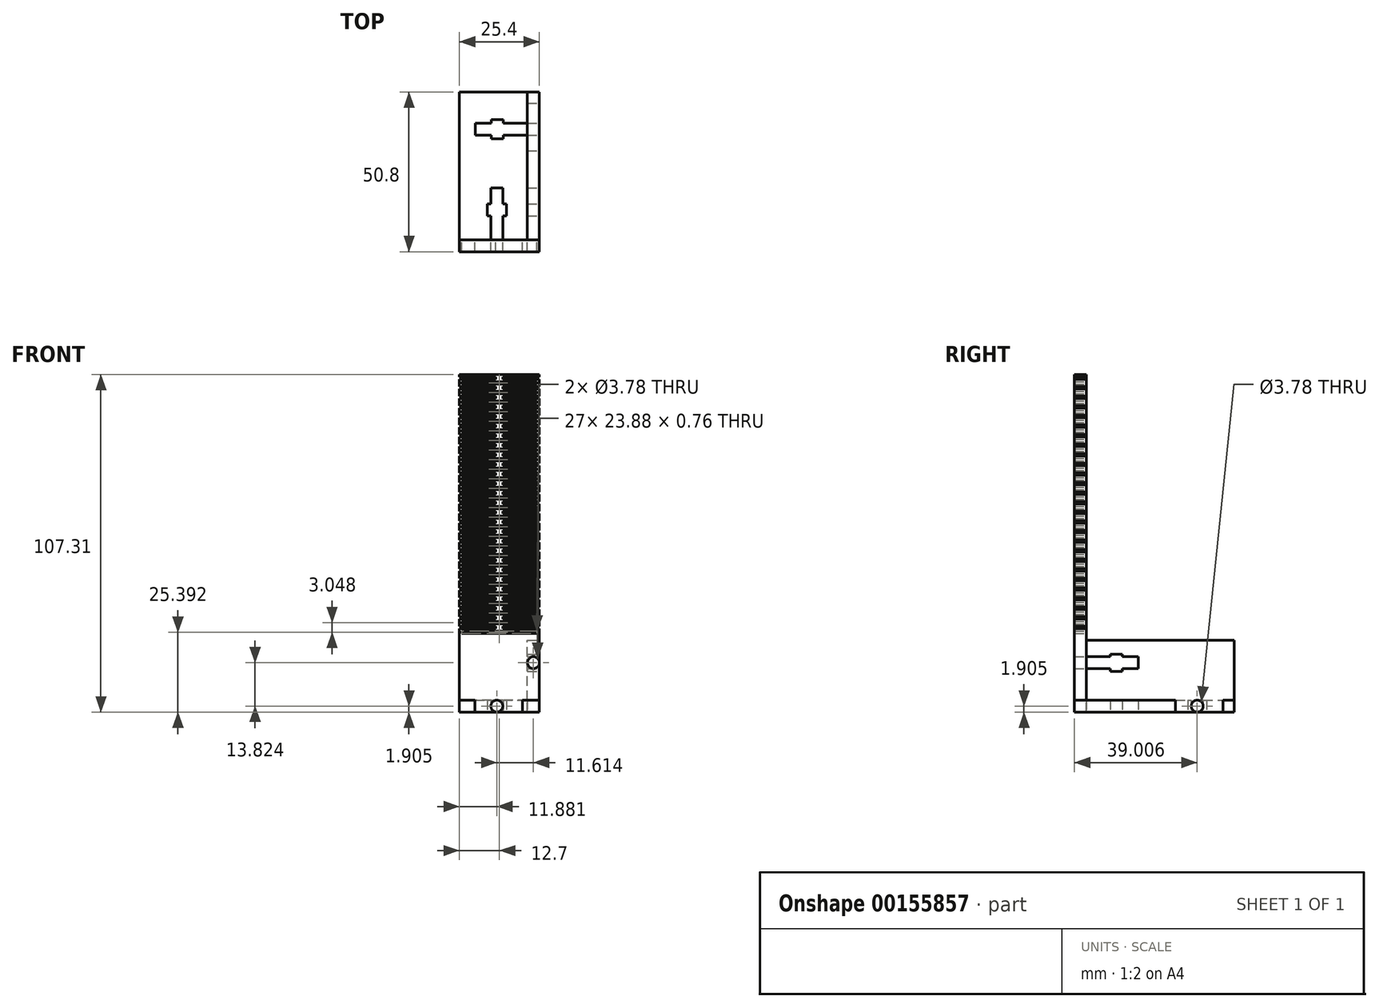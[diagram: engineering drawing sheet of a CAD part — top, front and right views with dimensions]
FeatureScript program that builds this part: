
annotation { "Feature Type Name" : "Feature", "Feature Type Description" : "" }
export const myFeature = defineFeature(function(context is Context, id is Id, definition is map)
    precondition{}
    {
        {
            var Q0;
            Q0=qCreatedBy(makeId("Top.planeOp"),FACE);
            var sketch = newSketch(context, id + "F0", { "sketchPlane" : qUnion([Q0])});
            skLineSegment(sketch, "E0.bottom", {"start": v(-25.4, -50.8) * mm, "end": v(-20.43, -50.8) * mm});
            skLineSegment(sketch, "E0.top", {"start": v(-25.4, 0) * mm, "end": v(0, 0) * mm});
            skLineSegment(sketch, "E0.left", {"start": v(-25.4, -50.8) * mm, "end": v(-25.4, 0) * mm});
            skLineSegment(sketch, "E0.right", {"start": v(0, -50.8) * mm, "end": v(0, -18.7) * mm});
            skLineSegment(sketch, "E1.bottom", {"start": v(-3.8, -9.89) * mm, "end": v(-11.43, -9.89) * mm});
            skLineSegment(sketch, "E1.top", {"start": v(-3.8, -13.7) * mm, "end": v(-11.43, -13.7) * mm});
            skLineSegment(sketch, "E1.right", {"start": v(-20.32, -9.89) * mm, "end": v(-20.32, -13.7) * mm});
            skLineSegment(sketch, "E2.bottom", {"start": v(-15.24, -14.83) * mm, "end": v(-11.43, -14.83) * mm});
            skLineSegment(sketch, "E2.top", {"start": v(-15.24, -8.76) * mm, "end": v(-11.43, -8.76) * mm});
            skLineSegment(sketch, "E2.left", {"start": v(-15.24, -14.83) * mm, "end": v(-15.24, -13.7) * mm});
            skLineSegment(sketch, "E2.right", {"start": v(-11.43, -14.83) * mm, "end": v(-11.43, -13.7) * mm});
            skLineSegment(sketch, "E3.trimOffspring", {"start": v(-11.43, -9.89) * mm, "end": v(-11.43, -8.76) * mm});
            skLineSegment(sketch, "E4.trimOffspring", {"start": v(-15.24, -9.89) * mm, "end": v(-15.24, -8.76) * mm});
            skLineSegment(sketch, "E5.trimOffspring", {"start": v(-15.24, -9.89) * mm, "end": v(-20.32, -9.89) * mm});
            skLineSegment(sketch, "E6.trimOffspring", {"start": v(-15.24, -13.7) * mm, "end": v(-20.32, -13.7) * mm});
            skLineSegment(sketch, "E7.bottom", {"start": v(0, -18.7) * mm, "end": v(-3.8, -18.7) * mm});
            skLineSegment(sketch, "E7.top", {"start": v(0, -3.62) * mm, "end": v(-3.8, -3.62) * mm});
            skLineSegment(sketch, "E7.right", {"start": v(-3.8, -18.7) * mm, "end": v(-3.8, -13.7) * mm});
            skLineSegment(sketch, "E8.trimOffspring", {"start": v(-3.8, -9.89) * mm, "end": v(-3.8, -3.62) * mm});
            skLineSegment(sketch, "E9.trimOffspring", {"start": v(0, -3.62) * mm, "end": v(0, 0) * mm});
            skLineSegment(sketch, "E10.bottom", {"start": v(-11.63, -46.99) * mm, "end": v(-11.63, -39.37) * mm});
            skLineSegment(sketch, "E10.top", {"start": v(-15.44, -46.99) * mm, "end": v(-15.44, -39.37) * mm});
            skLineSegment(sketch, "E10.right", {"start": v(-11.63, -30.48) * mm, "end": v(-15.44, -30.48) * mm});
            skLineSegment(sketch, "E11.bottom", {"start": v(-16.57, -35.56) * mm, "end": v(-16.57, -39.37) * mm});
            skLineSegment(sketch, "E11.top", {"start": v(-10.5, -35.56) * mm, "end": v(-10.5, -39.37) * mm});
            skLineSegment(sketch, "E11.left", {"start": v(-16.57, -35.56) * mm, "end": v(-15.44, -35.56) * mm});
            skLineSegment(sketch, "E11.right", {"start": v(-16.57, -39.37) * mm, "end": v(-15.44, -39.37) * mm});
            skLineSegment(sketch, "E12.trimOffspring", {"start": v(-11.63, -39.37) * mm, "end": v(-10.5, -39.37) * mm});
            skLineSegment(sketch, "E13.trimOffspring", {"start": v(-11.63, -35.56) * mm, "end": v(-10.5, -35.56) * mm});
            skLineSegment(sketch, "E14.trimOffspring", {"start": v(-11.63, -35.56) * mm, "end": v(-11.63, -30.48) * mm});
            skLineSegment(sketch, "E15.trimOffspring", {"start": v(-15.44, -35.56) * mm, "end": v(-15.44, -30.48) * mm});
            skLineSegment(sketch, "E16.bottom", {"start": v(-20.43, -50.8) * mm, "end": v(-20.43, -46.99) * mm});
            skLineSegment(sketch, "E16.top", {"start": v(-5.36, -50.8) * mm, "end": v(-5.36, -46.99) * mm});
            skLineSegment(sketch, "E16.right", {"start": v(-20.43, -46.99) * mm, "end": v(-15.44, -46.99) * mm});
            skLineSegment(sketch, "E17.trimOffspring", {"start": v(-11.63, -46.99) * mm, "end": v(-5.36, -46.99) * mm});
            skLineSegment(sketch, "E18.trimOffspring", {"start": v(-5.36, -50.8) * mm, "end": v(0, -50.8) * mm});
            skSolve(sketch);
        }
        {
            var Q0;
            Q0=makeQuery(id+"F0.imprint","IMPRINT",FACE,{"disambiguationData":[TD([[makeQuery(id+"F0.imprint","IMPRINT",EDGE,{"derivedFrom":sQuery(id+"F0.wireOp",EDGE,"E0.bottom")}),1.0]])]});
            extrude(context, id + "F1", {"entities" : qUnion([Q0]), "depth" : 3.8 * mm});
        }
        {
            var Q0;
            Q0=makeQuery(id+"F1.opExtrude","SWEPT_FACE",FACE,{"disambiguationData":[OSD([sQuery(id+"F0.wireOp",EDGE,"E16.right")])]});
            var sketch = newSketch(context, id + "F2", { "sketchPlane" : qUnion([Q0])});
            skLineSegment(sketch, "E19.bottom", {"start": v(-5.36, 0) * mm, "end": v(-20.43, 0) * mm});
            skLineSegment(sketch, "E20", {"start": v(-20.43, 0) * mm, "end": v(-20.43, 3.81) * mm});
            skLineSegment(sketch, "E21", {"start": v(-20.43, 3.81) * mm, "end": v(-25.4, 3.81) * mm});
            skLineSegment(sketch, "E22.MirrorCS", {"start": v(-5.36, 0) * mm, "end": v(-5.36, 3.81) * mm});
            skLineSegment(sketch, "E23.MirrorCS", {"start": v(-5.36, 3.81) * mm, "end": v(0, 3.81) * mm});
            skCircle(sketch, "E24", {"center": v(-13.52, 1.9) * mm, "radius": 1.9 * mm});
            skLineSegment(sketch, "E25", {"start": v(-20.43, 1.9) * mm, "end": v(-5.36, 1.9) * mm, "construction": true});
            skLineSegment(sketch, "E26", {"start": v(-25.4, 107.3) * mm, "end": v(-12.7, 107.3) * mm});
            skLineSegment(sketch, "E27", {"start": v(-12.7, 107.3) * mm, "end": v(-12.7, -12.92) * mm, "construction": true});
            skLineSegment(sketch, "E28.bottom", {"start": v(-25.4, 106.55) * mm, "end": v(-13.82, 106.55) * mm});
            skLineSegment(sketch, "E28.top", {"start": v(-25.4, 105.78) * mm, "end": v(-13.82, 105.78) * mm});
            skLineSegment(sketch, "E28.right", {"start": v(-13.82, 106.55) * mm, "end": v(-13.82, 105.78) * mm});
            skLineSegment(sketch, "E29.trimOffspring", {"start": v(-25.4, 106.55) * mm, "end": v(-25.4, 107.3) * mm});
            skPoint(sketch, "E30.start.orphan", {"position": v(0, 107.3) * mm});
            skLineSegment(sketch, "E31.MirrorCS", {"start": v(-11.58, 106.55) * mm, "end": v(-11.58, 105.78) * mm});
            skLineSegment(sketch, "E32.MirrorCS", {"start": v(0, 107.3) * mm, "end": v(-12.7, 107.3) * mm});
            skLineSegment(sketch, "E33.MirrorCS", {"start": v(0, 105.78) * mm, "end": v(-11.58, 105.78) * mm});
            skLineSegment(sketch, "E34.MirrorCS", {"start": v(0, 106.55) * mm, "end": v(0, 107.3) * mm});
            skLineSegment(sketch, "E35.MirrorCS", {"start": v(0, 106.55) * mm, "end": v(-11.58, 106.55) * mm});
            skLineSegment(sketch, "E36.bottom", {"start": v(-24.64, 105.02) * mm, "end": v(-0.76, 105.02) * mm});
            skLineSegment(sketch, "E36.top", {"start": v(-24.64, 104.26) * mm, "end": v(-0.76, 104.26) * mm});
            skLineSegment(sketch, "E36.left", {"start": v(-24.64, 105.02) * mm, "end": v(-24.64, 104.26) * mm});
            skLineSegment(sketch, "E36.right", {"start": v(-0.76, 105.02) * mm, "end": v(-0.76, 104.26) * mm});
            skLineSegment(sketch, "E37", {"start": v(-25.4, 105.78) * mm, "end": v(-25.4, 104.26) * mm});
            skLineSegment(sketch, "E38.MirrorCS", {"start": v(-38.1, 107.3) * mm, "end": v(-38.1, -12.92) * mm, "construction": true});
            skLineSegment(sketch, "E39.MirrorCS", {"start": v(0, 105.78) * mm, "end": v(0, 104.26) * mm});
            skLineSegment(sketch, "E40.0.1.0", {"start": v(-0.76, 101.97) * mm, "end": v(-0.76, 101.21) * mm});
            skLineSegment(sketch, "E40.0.1.1", {"start": v(0, 103.5) * mm, "end": v(0, 104.26) * mm});
            skPoint(sketch, "E40.0.1.2", {"position": v(0, 104.26) * mm});
            skLineSegment(sketch, "E40.0.1.3", {"start": v(-24.64, 101.97) * mm, "end": v(-24.64, 101.21) * mm});
            skLineSegment(sketch, "E40.0.1.4", {"start": v(0, 103.5) * mm, "end": v(-11.58, 103.5) * mm});
            skLineSegment(sketch, "E40.0.1.5", {"start": v(-25.4, 103.5) * mm, "end": v(-13.82, 103.5) * mm});
            skLineSegment(sketch, "E40.0.1.6", {"start": v(0, 102.74) * mm, "end": v(-11.58, 102.74) * mm});
            skLineSegment(sketch, "E40.0.1.7", {"start": v(0, 102.74) * mm, "end": v(0, 101.21) * mm});
            skLineSegment(sketch, "E40.0.1.8", {"start": v(-25.4, 102.74) * mm, "end": v(-25.4, 101.21) * mm});
            skLineSegment(sketch, "E40.0.1.9", {"start": v(-24.64, 101.21) * mm, "end": v(-0.76, 101.21) * mm});
            skLineSegment(sketch, "E40.0.1.10", {"start": v(-25.4, 103.5) * mm, "end": v(-25.4, 104.26) * mm});
            skLineSegment(sketch, "E40.0.1.11", {"start": v(-13.82, 103.5) * mm, "end": v(-13.82, 102.74) * mm});
            skLineSegment(sketch, "E40.0.1.12", {"start": v(-11.58, 103.5) * mm, "end": v(-11.58, 102.74) * mm});
            skLineSegment(sketch, "E40.0.1.13", {"start": v(-24.64, 101.97) * mm, "end": v(-0.76, 101.97) * mm});
            skLineSegment(sketch, "E40.0.1.14", {"start": v(-25.4, 102.74) * mm, "end": v(-13.82, 102.74) * mm});
            skLineSegment(sketch, "E40.0.2.0", {"start": v(-0.76, 98.93) * mm, "end": v(-0.76, 98.16) * mm});
            skLineSegment(sketch, "E40.0.2.1", {"start": v(0, 100.45) * mm, "end": v(0, 101.21) * mm});
            skPoint(sketch, "E40.0.2.2", {"position": v(0, 101.21) * mm});
            skLineSegment(sketch, "E40.0.2.3", {"start": v(-24.64, 98.93) * mm, "end": v(-24.64, 98.16) * mm});
            skLineSegment(sketch, "E40.0.2.4", {"start": v(0, 100.45) * mm, "end": v(-11.58, 100.45) * mm});
            skLineSegment(sketch, "E40.0.2.5", {"start": v(-25.4, 100.45) * mm, "end": v(-13.82, 100.45) * mm});
            skLineSegment(sketch, "E40.0.2.6", {"start": v(0, 99.69) * mm, "end": v(-11.58, 99.69) * mm});
            skLineSegment(sketch, "E40.0.2.7", {"start": v(0, 99.69) * mm, "end": v(0, 98.16) * mm});
            skLineSegment(sketch, "E40.0.2.8", {"start": v(-25.4, 99.69) * mm, "end": v(-25.4, 98.16) * mm});
            skLineSegment(sketch, "E40.0.2.9", {"start": v(-24.64, 98.16) * mm, "end": v(-0.76, 98.16) * mm});
            skLineSegment(sketch, "E40.0.2.10", {"start": v(-25.4, 100.45) * mm, "end": v(-25.4, 101.21) * mm});
            skLineSegment(sketch, "E40.0.2.11", {"start": v(-13.82, 100.45) * mm, "end": v(-13.82, 99.69) * mm});
            skLineSegment(sketch, "E40.0.2.12", {"start": v(-11.58, 100.45) * mm, "end": v(-11.58, 99.69) * mm});
            skLineSegment(sketch, "E40.0.2.13", {"start": v(-24.64, 98.93) * mm, "end": v(-0.76, 98.93) * mm});
            skLineSegment(sketch, "E40.0.2.14", {"start": v(-25.4, 99.69) * mm, "end": v(-13.82, 99.69) * mm});
            skLineSegment(sketch, "E40.0.3.0", {"start": v(-0.76, 95.88) * mm, "end": v(-0.76, 95.12) * mm});
            skLineSegment(sketch, "E40.0.3.1", {"start": v(0, 97.4) * mm, "end": v(0, 98.16) * mm});
            skPoint(sketch, "E40.0.3.2", {"position": v(0, 98.16) * mm});
            skLineSegment(sketch, "E40.0.3.3", {"start": v(-24.64, 95.88) * mm, "end": v(-24.64, 95.12) * mm});
            skLineSegment(sketch, "E40.0.3.4", {"start": v(0, 97.4) * mm, "end": v(-11.58, 97.4) * mm});
            skLineSegment(sketch, "E40.0.3.5", {"start": v(-25.4, 97.4) * mm, "end": v(-13.82, 97.4) * mm});
            skLineSegment(sketch, "E40.0.3.6", {"start": v(0, 96.64) * mm, "end": v(-11.58, 96.64) * mm});
            skLineSegment(sketch, "E40.0.3.7", {"start": v(0, 96.64) * mm, "end": v(0, 95.12) * mm});
            skLineSegment(sketch, "E40.0.3.8", {"start": v(-25.4, 96.64) * mm, "end": v(-25.4, 95.12) * mm});
            skLineSegment(sketch, "E40.0.3.9", {"start": v(-24.64, 95.12) * mm, "end": v(-0.76, 95.12) * mm});
            skLineSegment(sketch, "E40.0.3.10", {"start": v(-25.4, 97.4) * mm, "end": v(-25.4, 98.16) * mm});
            skLineSegment(sketch, "E40.0.3.11", {"start": v(-13.82, 97.4) * mm, "end": v(-13.82, 96.64) * mm});
            skLineSegment(sketch, "E40.0.3.12", {"start": v(-11.58, 97.4) * mm, "end": v(-11.58, 96.64) * mm});
            skLineSegment(sketch, "E40.0.3.13", {"start": v(-24.64, 95.88) * mm, "end": v(-0.76, 95.88) * mm});
            skLineSegment(sketch, "E40.0.3.14", {"start": v(-25.4, 96.64) * mm, "end": v(-13.82, 96.64) * mm});
            skLineSegment(sketch, "E40.0.4.0", {"start": v(-0.76, 92.83) * mm, "end": v(-0.76, 92.07) * mm});
            skLineSegment(sketch, "E40.0.4.1", {"start": v(0, 94.35) * mm, "end": v(0, 95.12) * mm});
            skPoint(sketch, "E40.0.4.2", {"position": v(0, 95.12) * mm});
            skLineSegment(sketch, "E40.0.4.3", {"start": v(-24.64, 92.83) * mm, "end": v(-24.64, 92.07) * mm});
            skLineSegment(sketch, "E40.0.4.4", {"start": v(0, 94.35) * mm, "end": v(-11.58, 94.35) * mm});
            skLineSegment(sketch, "E40.0.4.5", {"start": v(-25.4, 94.35) * mm, "end": v(-13.82, 94.35) * mm});
            skLineSegment(sketch, "E40.0.4.6", {"start": v(0, 93.6) * mm, "end": v(-11.58, 93.6) * mm});
            skLineSegment(sketch, "E40.0.4.7", {"start": v(0, 93.6) * mm, "end": v(0, 92.07) * mm});
            skLineSegment(sketch, "E40.0.4.8", {"start": v(-25.4, 93.6) * mm, "end": v(-25.4, 92.07) * mm});
            skLineSegment(sketch, "E40.0.4.9", {"start": v(-24.64, 92.07) * mm, "end": v(-0.76, 92.07) * mm});
            skLineSegment(sketch, "E40.0.4.10", {"start": v(-25.4, 94.35) * mm, "end": v(-25.4, 95.12) * mm});
            skLineSegment(sketch, "E40.0.4.11", {"start": v(-13.82, 94.35) * mm, "end": v(-13.82, 93.6) * mm});
            skLineSegment(sketch, "E40.0.4.12", {"start": v(-11.58, 94.35) * mm, "end": v(-11.58, 93.6) * mm});
            skLineSegment(sketch, "E40.0.4.13", {"start": v(-24.64, 92.83) * mm, "end": v(-0.76, 92.83) * mm});
            skLineSegment(sketch, "E40.0.4.14", {"start": v(-25.4, 93.6) * mm, "end": v(-13.82, 93.6) * mm});
            skLineSegment(sketch, "E40.0.5.0", {"start": v(-0.76, 89.78) * mm, "end": v(-0.76, 89.02) * mm});
            skLineSegment(sketch, "E40.0.5.1", {"start": v(0, 91.3) * mm, "end": v(0, 92.07) * mm});
            skPoint(sketch, "E40.0.5.2", {"position": v(0, 92.07) * mm});
            skLineSegment(sketch, "E40.0.5.3", {"start": v(-24.64, 89.78) * mm, "end": v(-24.64, 89.02) * mm});
            skLineSegment(sketch, "E40.0.5.4", {"start": v(0, 91.3) * mm, "end": v(-11.58, 91.3) * mm});
            skLineSegment(sketch, "E40.0.5.5", {"start": v(-25.4, 91.3) * mm, "end": v(-13.82, 91.3) * mm});
            skLineSegment(sketch, "E40.0.5.6", {"start": v(0, 90.54) * mm, "end": v(-11.58, 90.54) * mm});
            skLineSegment(sketch, "E40.0.5.7", {"start": v(0, 90.54) * mm, "end": v(0, 89.02) * mm});
            skLineSegment(sketch, "E40.0.5.8", {"start": v(-25.4, 90.54) * mm, "end": v(-25.4, 89.02) * mm});
            skLineSegment(sketch, "E40.0.5.9", {"start": v(-24.64, 89.02) * mm, "end": v(-0.76, 89.02) * mm});
            skLineSegment(sketch, "E40.0.5.10", {"start": v(-25.4, 91.3) * mm, "end": v(-25.4, 92.07) * mm});
            skLineSegment(sketch, "E40.0.5.11", {"start": v(-13.82, 91.3) * mm, "end": v(-13.82, 90.54) * mm});
            skLineSegment(sketch, "E40.0.5.12", {"start": v(-11.58, 91.3) * mm, "end": v(-11.58, 90.54) * mm});
            skLineSegment(sketch, "E40.0.5.13", {"start": v(-24.64, 89.78) * mm, "end": v(-0.76, 89.78) * mm});
            skLineSegment(sketch, "E40.0.5.14", {"start": v(-25.4, 90.54) * mm, "end": v(-13.82, 90.54) * mm});
            skLineSegment(sketch, "E40.0.6.0", {"start": v(-0.76, 86.73) * mm, "end": v(-0.76, 85.97) * mm});
            skLineSegment(sketch, "E40.0.6.1", {"start": v(0, 88.26) * mm, "end": v(0, 89.02) * mm});
            skPoint(sketch, "E40.0.6.2", {"position": v(0, 89.02) * mm});
            skLineSegment(sketch, "E40.0.6.3", {"start": v(-24.64, 86.73) * mm, "end": v(-24.64, 85.97) * mm});
            skLineSegment(sketch, "E40.0.6.4", {"start": v(0, 88.26) * mm, "end": v(-11.58, 88.26) * mm});
            skLineSegment(sketch, "E40.0.6.5", {"start": v(-25.4, 88.26) * mm, "end": v(-13.82, 88.26) * mm});
            skLineSegment(sketch, "E40.0.6.6", {"start": v(0, 87.5) * mm, "end": v(-11.58, 87.5) * mm});
            skLineSegment(sketch, "E40.0.6.7", {"start": v(0, 87.5) * mm, "end": v(0, 85.97) * mm});
            skLineSegment(sketch, "E40.0.6.8", {"start": v(-25.4, 87.5) * mm, "end": v(-25.4, 85.97) * mm});
            skLineSegment(sketch, "E40.0.6.9", {"start": v(-24.64, 85.97) * mm, "end": v(-0.76, 85.97) * mm});
            skLineSegment(sketch, "E40.0.6.10", {"start": v(-25.4, 88.26) * mm, "end": v(-25.4, 89.02) * mm});
            skLineSegment(sketch, "E40.0.6.11", {"start": v(-13.82, 88.26) * mm, "end": v(-13.82, 87.5) * mm});
            skLineSegment(sketch, "E40.0.6.12", {"start": v(-11.58, 88.26) * mm, "end": v(-11.58, 87.5) * mm});
            skLineSegment(sketch, "E40.0.6.13", {"start": v(-24.64, 86.73) * mm, "end": v(-0.76, 86.73) * mm});
            skLineSegment(sketch, "E40.0.6.14", {"start": v(-25.4, 87.5) * mm, "end": v(-13.82, 87.5) * mm});
            skLineSegment(sketch, "E40.0.7.0", {"start": v(-0.76, 83.69) * mm, "end": v(-0.76, 82.92) * mm});
            skLineSegment(sketch, "E40.0.7.1", {"start": v(0, 85.2) * mm, "end": v(0, 85.97) * mm});
            skPoint(sketch, "E40.0.7.2", {"position": v(0, 85.97) * mm});
            skLineSegment(sketch, "E40.0.7.3", {"start": v(-24.64, 83.69) * mm, "end": v(-24.64, 82.92) * mm});
            skLineSegment(sketch, "E40.0.7.4", {"start": v(0, 85.2) * mm, "end": v(-11.58, 85.2) * mm});
            skLineSegment(sketch, "E40.0.7.5", {"start": v(-25.4, 85.2) * mm, "end": v(-13.82, 85.2) * mm});
            skLineSegment(sketch, "E40.0.7.6", {"start": v(0, 84.45) * mm, "end": v(-11.58, 84.45) * mm});
            skLineSegment(sketch, "E40.0.7.7", {"start": v(0, 84.45) * mm, "end": v(0, 82.92) * mm});
            skLineSegment(sketch, "E40.0.7.8", {"start": v(-25.4, 84.45) * mm, "end": v(-25.4, 82.92) * mm});
            skLineSegment(sketch, "E40.0.7.9", {"start": v(-24.64, 82.92) * mm, "end": v(-0.76, 82.92) * mm});
            skLineSegment(sketch, "E40.0.7.10", {"start": v(-25.4, 85.2) * mm, "end": v(-25.4, 85.97) * mm});
            skLineSegment(sketch, "E40.0.7.11", {"start": v(-13.82, 85.2) * mm, "end": v(-13.82, 84.45) * mm});
            skLineSegment(sketch, "E40.0.7.12", {"start": v(-11.58, 85.2) * mm, "end": v(-11.58, 84.45) * mm});
            skLineSegment(sketch, "E40.0.7.13", {"start": v(-24.64, 83.69) * mm, "end": v(-0.76, 83.69) * mm});
            skLineSegment(sketch, "E40.0.7.14", {"start": v(-25.4, 84.45) * mm, "end": v(-13.82, 84.45) * mm});
            skLineSegment(sketch, "E40.0.8.0", {"start": v(-0.76, 80.64) * mm, "end": v(-0.76, 79.88) * mm});
            skLineSegment(sketch, "E40.0.8.1", {"start": v(0, 82.16) * mm, "end": v(0, 82.92) * mm});
            skPoint(sketch, "E40.0.8.2", {"position": v(0, 82.92) * mm});
            skLineSegment(sketch, "E40.0.8.3", {"start": v(-24.64, 80.64) * mm, "end": v(-24.64, 79.88) * mm});
            skLineSegment(sketch, "E40.0.8.4", {"start": v(0, 82.16) * mm, "end": v(-11.58, 82.16) * mm});
            skLineSegment(sketch, "E40.0.8.5", {"start": v(-25.4, 82.16) * mm, "end": v(-13.82, 82.16) * mm});
            skLineSegment(sketch, "E40.0.8.6", {"start": v(0, 81.4) * mm, "end": v(-11.58, 81.4) * mm});
            skLineSegment(sketch, "E40.0.8.7", {"start": v(0, 81.4) * mm, "end": v(0, 79.88) * mm});
            skLineSegment(sketch, "E40.0.8.8", {"start": v(-25.4, 81.4) * mm, "end": v(-25.4, 79.88) * mm});
            skLineSegment(sketch, "E40.0.8.9", {"start": v(-24.64, 79.88) * mm, "end": v(-0.76, 79.88) * mm});
            skLineSegment(sketch, "E40.0.8.10", {"start": v(-25.4, 82.16) * mm, "end": v(-25.4, 82.92) * mm});
            skLineSegment(sketch, "E40.0.8.11", {"start": v(-13.82, 82.16) * mm, "end": v(-13.82, 81.4) * mm});
            skLineSegment(sketch, "E40.0.8.12", {"start": v(-11.58, 82.16) * mm, "end": v(-11.58, 81.4) * mm});
            skLineSegment(sketch, "E40.0.8.13", {"start": v(-24.64, 80.64) * mm, "end": v(-0.76, 80.64) * mm});
            skLineSegment(sketch, "E40.0.8.14", {"start": v(-25.4, 81.4) * mm, "end": v(-13.82, 81.4) * mm});
            skLineSegment(sketch, "E40.0.9.0", {"start": v(-0.76, 77.59) * mm, "end": v(-0.76, 76.83) * mm});
            skLineSegment(sketch, "E40.0.9.1", {"start": v(0, 79.11) * mm, "end": v(0, 79.88) * mm});
            skPoint(sketch, "E40.0.9.2", {"position": v(0, 79.88) * mm});
            skLineSegment(sketch, "E40.0.9.3", {"start": v(-24.64, 77.59) * mm, "end": v(-24.64, 76.83) * mm});
            skLineSegment(sketch, "E40.0.9.4", {"start": v(0, 79.11) * mm, "end": v(-11.58, 79.11) * mm});
            skLineSegment(sketch, "E40.0.9.5", {"start": v(-25.4, 79.11) * mm, "end": v(-13.82, 79.11) * mm});
            skLineSegment(sketch, "E40.0.9.6", {"start": v(0, 78.35) * mm, "end": v(-11.58, 78.35) * mm});
            skLineSegment(sketch, "E40.0.9.7", {"start": v(0, 78.35) * mm, "end": v(0, 76.83) * mm});
            skLineSegment(sketch, "E40.0.9.8", {"start": v(-25.4, 78.35) * mm, "end": v(-25.4, 76.83) * mm});
            skLineSegment(sketch, "E40.0.9.9", {"start": v(-24.64, 76.83) * mm, "end": v(-0.76, 76.83) * mm});
            skLineSegment(sketch, "E40.0.9.10", {"start": v(-25.4, 79.11) * mm, "end": v(-25.4, 79.88) * mm});
            skLineSegment(sketch, "E40.0.9.11", {"start": v(-13.82, 79.11) * mm, "end": v(-13.82, 78.35) * mm});
            skLineSegment(sketch, "E40.0.9.12", {"start": v(-11.58, 79.11) * mm, "end": v(-11.58, 78.35) * mm});
            skLineSegment(sketch, "E40.0.9.13", {"start": v(-24.64, 77.59) * mm, "end": v(-0.76, 77.59) * mm});
            skLineSegment(sketch, "E40.0.9.14", {"start": v(-25.4, 78.35) * mm, "end": v(-13.82, 78.35) * mm});
            skLineSegment(sketch, "E40.0.10.0", {"start": v(-0.76, 74.54) * mm, "end": v(-0.76, 73.78) * mm});
            skLineSegment(sketch, "E40.0.10.1", {"start": v(0, 76.07) * mm, "end": v(0, 76.83) * mm});
            skPoint(sketch, "E40.0.10.2", {"position": v(0, 76.83) * mm});
            skLineSegment(sketch, "E40.0.10.3", {"start": v(-24.64, 74.54) * mm, "end": v(-24.64, 73.78) * mm});
            skLineSegment(sketch, "E40.0.10.4", {"start": v(0, 76.07) * mm, "end": v(-11.58, 76.07) * mm});
            skLineSegment(sketch, "E40.0.10.5", {"start": v(-25.4, 76.07) * mm, "end": v(-13.82, 76.07) * mm});
            skLineSegment(sketch, "E40.0.10.6", {"start": v(0, 75.3) * mm, "end": v(-11.58, 75.3) * mm});
            skLineSegment(sketch, "E40.0.10.7", {"start": v(0, 75.3) * mm, "end": v(0, 73.78) * mm});
            skLineSegment(sketch, "E40.0.10.8", {"start": v(-25.4, 75.3) * mm, "end": v(-25.4, 73.78) * mm});
            skLineSegment(sketch, "E40.0.10.9", {"start": v(-24.64, 73.78) * mm, "end": v(-0.76, 73.78) * mm});
            skLineSegment(sketch, "E40.0.10.10", {"start": v(-25.4, 76.07) * mm, "end": v(-25.4, 76.83) * mm});
            skLineSegment(sketch, "E40.0.10.11", {"start": v(-13.82, 76.07) * mm, "end": v(-13.82, 75.3) * mm});
            skLineSegment(sketch, "E40.0.10.12", {"start": v(-11.58, 76.07) * mm, "end": v(-11.58, 75.3) * mm});
            skLineSegment(sketch, "E40.0.10.13", {"start": v(-24.64, 74.54) * mm, "end": v(-0.76, 74.54) * mm});
            skLineSegment(sketch, "E40.0.10.14", {"start": v(-25.4, 75.3) * mm, "end": v(-13.82, 75.3) * mm});
            skLineSegment(sketch, "E40.0.11.0", {"start": v(-0.76, 71.5) * mm, "end": v(-0.76, 70.73) * mm});
            skLineSegment(sketch, "E40.0.11.1", {"start": v(0, 73.02) * mm, "end": v(0, 73.78) * mm});
            skPoint(sketch, "E40.0.11.2", {"position": v(0, 73.78) * mm});
            skLineSegment(sketch, "E40.0.11.3", {"start": v(-24.64, 71.5) * mm, "end": v(-24.64, 70.73) * mm});
            skLineSegment(sketch, "E40.0.11.4", {"start": v(0, 73.02) * mm, "end": v(-11.58, 73.02) * mm});
            skLineSegment(sketch, "E40.0.11.5", {"start": v(-25.4, 73.02) * mm, "end": v(-13.82, 73.02) * mm});
            skLineSegment(sketch, "E40.0.11.6", {"start": v(0, 72.26) * mm, "end": v(-11.58, 72.26) * mm});
            skLineSegment(sketch, "E40.0.11.7", {"start": v(0, 72.26) * mm, "end": v(0, 70.73) * mm});
            skLineSegment(sketch, "E40.0.11.8", {"start": v(-25.4, 72.26) * mm, "end": v(-25.4, 70.73) * mm});
            skLineSegment(sketch, "E40.0.11.9", {"start": v(-24.64, 70.73) * mm, "end": v(-0.76, 70.73) * mm});
            skLineSegment(sketch, "E40.0.11.10", {"start": v(-25.4, 73.02) * mm, "end": v(-25.4, 73.78) * mm});
            skLineSegment(sketch, "E40.0.11.11", {"start": v(-13.82, 73.02) * mm, "end": v(-13.82, 72.26) * mm});
            skLineSegment(sketch, "E40.0.11.12", {"start": v(-11.58, 73.02) * mm, "end": v(-11.58, 72.26) * mm});
            skLineSegment(sketch, "E40.0.11.13", {"start": v(-24.64, 71.5) * mm, "end": v(-0.76, 71.5) * mm});
            skLineSegment(sketch, "E40.0.11.14", {"start": v(-25.4, 72.26) * mm, "end": v(-13.82, 72.26) * mm});
            skLineSegment(sketch, "E40.0.12.0", {"start": v(-0.76, 68.45) * mm, "end": v(-0.76, 67.68) * mm});
            skLineSegment(sketch, "E40.0.12.1", {"start": v(0, 69.97) * mm, "end": v(0, 70.73) * mm});
            skPoint(sketch, "E40.0.12.2", {"position": v(0, 70.73) * mm});
            skLineSegment(sketch, "E40.0.12.3", {"start": v(-24.64, 68.45) * mm, "end": v(-24.64, 67.68) * mm});
            skLineSegment(sketch, "E40.0.12.4", {"start": v(0, 69.97) * mm, "end": v(-11.58, 69.97) * mm});
            skLineSegment(sketch, "E40.0.12.5", {"start": v(-25.4, 69.97) * mm, "end": v(-13.82, 69.97) * mm});
            skLineSegment(sketch, "E40.0.12.6", {"start": v(0, 69.2) * mm, "end": v(-11.58, 69.2) * mm});
            skLineSegment(sketch, "E40.0.12.7", {"start": v(0, 69.2) * mm, "end": v(0, 67.68) * mm});
            skLineSegment(sketch, "E40.0.12.8", {"start": v(-25.4, 69.2) * mm, "end": v(-25.4, 67.68) * mm});
            skLineSegment(sketch, "E40.0.12.9", {"start": v(-24.64, 67.68) * mm, "end": v(-0.76, 67.68) * mm});
            skLineSegment(sketch, "E40.0.12.10", {"start": v(-25.4, 69.97) * mm, "end": v(-25.4, 70.73) * mm});
            skLineSegment(sketch, "E40.0.12.11", {"start": v(-13.82, 69.97) * mm, "end": v(-13.82, 69.2) * mm});
            skLineSegment(sketch, "E40.0.12.12", {"start": v(-11.58, 69.97) * mm, "end": v(-11.58, 69.2) * mm});
            skLineSegment(sketch, "E40.0.12.13", {"start": v(-24.64, 68.45) * mm, "end": v(-0.76, 68.45) * mm});
            skLineSegment(sketch, "E40.0.12.14", {"start": v(-25.4, 69.2) * mm, "end": v(-13.82, 69.2) * mm});
            skLineSegment(sketch, "E40.0.13.0", {"start": v(-0.76, 65.4) * mm, "end": v(-0.76, 64.64) * mm});
            skLineSegment(sketch, "E40.0.13.1", {"start": v(0, 66.92) * mm, "end": v(0, 67.68) * mm});
            skPoint(sketch, "E40.0.13.2", {"position": v(0, 67.68) * mm});
            skLineSegment(sketch, "E40.0.13.3", {"start": v(-24.64, 65.4) * mm, "end": v(-24.64, 64.64) * mm});
            skLineSegment(sketch, "E40.0.13.4", {"start": v(0, 66.92) * mm, "end": v(-11.58, 66.92) * mm});
            skLineSegment(sketch, "E40.0.13.5", {"start": v(-25.4, 66.92) * mm, "end": v(-13.82, 66.92) * mm});
            skLineSegment(sketch, "E40.0.13.6", {"start": v(0, 66.16) * mm, "end": v(-11.58, 66.16) * mm});
            skLineSegment(sketch, "E40.0.13.7", {"start": v(0, 66.16) * mm, "end": v(0, 64.64) * mm});
            skLineSegment(sketch, "E40.0.13.8", {"start": v(-25.4, 66.16) * mm, "end": v(-25.4, 64.64) * mm});
            skLineSegment(sketch, "E40.0.13.9", {"start": v(-24.64, 64.64) * mm, "end": v(-0.76, 64.64) * mm});
            skLineSegment(sketch, "E40.0.13.10", {"start": v(-25.4, 66.92) * mm, "end": v(-25.4, 67.68) * mm});
            skLineSegment(sketch, "E40.0.13.11", {"start": v(-13.82, 66.92) * mm, "end": v(-13.82, 66.16) * mm});
            skLineSegment(sketch, "E40.0.13.12", {"start": v(-11.58, 66.92) * mm, "end": v(-11.58, 66.16) * mm});
            skLineSegment(sketch, "E40.0.13.13", {"start": v(-24.64, 65.4) * mm, "end": v(-0.76, 65.4) * mm});
            skLineSegment(sketch, "E40.0.13.14", {"start": v(-25.4, 66.16) * mm, "end": v(-13.82, 66.16) * mm});
            skLineSegment(sketch, "E40.0.14.0", {"start": v(-0.76, 62.35) * mm, "end": v(-0.76, 61.59) * mm});
            skLineSegment(sketch, "E40.0.14.1", {"start": v(0, 63.87) * mm, "end": v(0, 64.64) * mm});
            skPoint(sketch, "E40.0.14.2", {"position": v(0, 64.64) * mm});
            skLineSegment(sketch, "E40.0.14.3", {"start": v(-24.64, 62.35) * mm, "end": v(-24.64, 61.59) * mm});
            skLineSegment(sketch, "E40.0.14.4", {"start": v(0, 63.87) * mm, "end": v(-11.58, 63.87) * mm});
            skLineSegment(sketch, "E40.0.14.5", {"start": v(-25.4, 63.87) * mm, "end": v(-13.82, 63.87) * mm});
            skLineSegment(sketch, "E40.0.14.6", {"start": v(0, 63.11) * mm, "end": v(-11.58, 63.11) * mm});
            skLineSegment(sketch, "E40.0.14.7", {"start": v(0, 63.11) * mm, "end": v(0, 61.59) * mm});
            skLineSegment(sketch, "E40.0.14.8", {"start": v(-25.4, 63.11) * mm, "end": v(-25.4, 61.59) * mm});
            skLineSegment(sketch, "E40.0.14.9", {"start": v(-24.64, 61.59) * mm, "end": v(-0.76, 61.59) * mm});
            skLineSegment(sketch, "E40.0.14.10", {"start": v(-25.4, 63.87) * mm, "end": v(-25.4, 64.64) * mm});
            skLineSegment(sketch, "E40.0.14.11", {"start": v(-13.82, 63.87) * mm, "end": v(-13.82, 63.11) * mm});
            skLineSegment(sketch, "E40.0.14.12", {"start": v(-11.58, 63.87) * mm, "end": v(-11.58, 63.11) * mm});
            skLineSegment(sketch, "E40.0.14.13", {"start": v(-24.64, 62.35) * mm, "end": v(-0.76, 62.35) * mm});
            skLineSegment(sketch, "E40.0.14.14", {"start": v(-25.4, 63.11) * mm, "end": v(-13.82, 63.11) * mm});
            skLineSegment(sketch, "E40.0.15.0", {"start": v(-0.76, 59.3) * mm, "end": v(-0.76, 58.54) * mm});
            skLineSegment(sketch, "E40.0.15.1", {"start": v(0, 60.83) * mm, "end": v(0, 61.59) * mm});
            skPoint(sketch, "E40.0.15.2", {"position": v(0, 61.59) * mm});
            skLineSegment(sketch, "E40.0.15.3", {"start": v(-24.64, 59.3) * mm, "end": v(-24.64, 58.54) * mm});
            skLineSegment(sketch, "E40.0.15.4", {"start": v(0, 60.83) * mm, "end": v(-11.58, 60.83) * mm});
            skLineSegment(sketch, "E40.0.15.5", {"start": v(-25.4, 60.83) * mm, "end": v(-13.82, 60.83) * mm});
            skLineSegment(sketch, "E40.0.15.6", {"start": v(0, 60.06) * mm, "end": v(-11.58, 60.06) * mm});
            skLineSegment(sketch, "E40.0.15.7", {"start": v(0, 60.06) * mm, "end": v(0, 58.54) * mm});
            skLineSegment(sketch, "E40.0.15.8", {"start": v(-25.4, 60.06) * mm, "end": v(-25.4, 58.54) * mm});
            skLineSegment(sketch, "E40.0.15.9", {"start": v(-24.64, 58.54) * mm, "end": v(-0.76, 58.54) * mm});
            skLineSegment(sketch, "E40.0.15.10", {"start": v(-25.4, 60.83) * mm, "end": v(-25.4, 61.59) * mm});
            skLineSegment(sketch, "E40.0.15.11", {"start": v(-13.82, 60.83) * mm, "end": v(-13.82, 60.06) * mm});
            skLineSegment(sketch, "E40.0.15.12", {"start": v(-11.58, 60.83) * mm, "end": v(-11.58, 60.06) * mm});
            skLineSegment(sketch, "E40.0.15.13", {"start": v(-24.64, 59.3) * mm, "end": v(-0.76, 59.3) * mm});
            skLineSegment(sketch, "E40.0.15.14", {"start": v(-25.4, 60.06) * mm, "end": v(-13.82, 60.06) * mm});
            skLineSegment(sketch, "E40.0.16.0", {"start": v(-0.76, 56.25) * mm, "end": v(-0.76, 55.5) * mm});
            skLineSegment(sketch, "E40.0.16.1", {"start": v(0, 57.78) * mm, "end": v(0, 58.54) * mm});
            skPoint(sketch, "E40.0.16.2", {"position": v(0, 58.54) * mm});
            skLineSegment(sketch, "E40.0.16.3", {"start": v(-24.64, 56.25) * mm, "end": v(-24.64, 55.5) * mm});
            skLineSegment(sketch, "E40.0.16.4", {"start": v(0, 57.78) * mm, "end": v(-11.58, 57.78) * mm});
            skLineSegment(sketch, "E40.0.16.5", {"start": v(-25.4, 57.78) * mm, "end": v(-13.82, 57.78) * mm});
            skLineSegment(sketch, "E40.0.16.6", {"start": v(0, 57.02) * mm, "end": v(-11.58, 57.02) * mm});
            skLineSegment(sketch, "E40.0.16.7", {"start": v(0, 57.02) * mm, "end": v(0, 55.5) * mm});
            skLineSegment(sketch, "E40.0.16.8", {"start": v(-25.4, 57.02) * mm, "end": v(-25.4, 55.5) * mm});
            skLineSegment(sketch, "E40.0.16.9", {"start": v(-24.64, 55.5) * mm, "end": v(-0.76, 55.5) * mm});
            skLineSegment(sketch, "E40.0.16.10", {"start": v(-25.4, 57.78) * mm, "end": v(-25.4, 58.54) * mm});
            skLineSegment(sketch, "E40.0.16.11", {"start": v(-13.82, 57.78) * mm, "end": v(-13.82, 57.02) * mm});
            skLineSegment(sketch, "E40.0.16.12", {"start": v(-11.58, 57.78) * mm, "end": v(-11.58, 57.02) * mm});
            skLineSegment(sketch, "E40.0.16.13", {"start": v(-24.64, 56.25) * mm, "end": v(-0.76, 56.25) * mm});
            skLineSegment(sketch, "E40.0.16.14", {"start": v(-25.4, 57.02) * mm, "end": v(-13.82, 57.02) * mm});
            skLineSegment(sketch, "E40.0.17.0", {"start": v(-0.76, 53.2) * mm, "end": v(-0.76, 52.44) * mm});
            skLineSegment(sketch, "E40.0.17.1", {"start": v(0, 54.73) * mm, "end": v(0, 55.5) * mm});
            skPoint(sketch, "E40.0.17.2", {"position": v(0, 55.5) * mm});
            skLineSegment(sketch, "E40.0.17.3", {"start": v(-24.64, 53.2) * mm, "end": v(-24.64, 52.44) * mm});
            skLineSegment(sketch, "E40.0.17.4", {"start": v(0, 54.73) * mm, "end": v(-11.58, 54.73) * mm});
            skLineSegment(sketch, "E40.0.17.5", {"start": v(-25.4, 54.73) * mm, "end": v(-13.82, 54.73) * mm});
            skLineSegment(sketch, "E40.0.17.6", {"start": v(0, 53.97) * mm, "end": v(-11.58, 53.97) * mm});
            skLineSegment(sketch, "E40.0.17.7", {"start": v(0, 53.97) * mm, "end": v(0, 52.44) * mm});
            skLineSegment(sketch, "E40.0.17.8", {"start": v(-25.4, 53.97) * mm, "end": v(-25.4, 52.44) * mm});
            skLineSegment(sketch, "E40.0.17.9", {"start": v(-24.64, 52.44) * mm, "end": v(-0.76, 52.44) * mm});
            skLineSegment(sketch, "E40.0.17.10", {"start": v(-25.4, 54.73) * mm, "end": v(-25.4, 55.5) * mm});
            skLineSegment(sketch, "E40.0.17.11", {"start": v(-13.82, 54.73) * mm, "end": v(-13.82, 53.97) * mm});
            skLineSegment(sketch, "E40.0.17.12", {"start": v(-11.58, 54.73) * mm, "end": v(-11.58, 53.97) * mm});
            skLineSegment(sketch, "E40.0.17.13", {"start": v(-24.64, 53.2) * mm, "end": v(-0.76, 53.2) * mm});
            skLineSegment(sketch, "E40.0.17.14", {"start": v(-25.4, 53.97) * mm, "end": v(-13.82, 53.97) * mm});
            skLineSegment(sketch, "E40.0.18.0", {"start": v(-0.76, 50.16) * mm, "end": v(-0.76, 49.4) * mm});
            skLineSegment(sketch, "E40.0.18.1", {"start": v(0, 51.68) * mm, "end": v(0, 52.44) * mm});
            skPoint(sketch, "E40.0.18.2", {"position": v(0, 52.44) * mm});
            skLineSegment(sketch, "E40.0.18.3", {"start": v(-24.64, 50.16) * mm, "end": v(-24.64, 49.4) * mm});
            skLineSegment(sketch, "E40.0.18.4", {"start": v(0, 51.68) * mm, "end": v(-11.58, 51.68) * mm});
            skLineSegment(sketch, "E40.0.18.5", {"start": v(-25.4, 51.68) * mm, "end": v(-13.82, 51.68) * mm});
            skLineSegment(sketch, "E40.0.18.6", {"start": v(0, 50.92) * mm, "end": v(-11.58, 50.92) * mm});
            skLineSegment(sketch, "E40.0.18.7", {"start": v(0, 50.92) * mm, "end": v(0, 49.4) * mm});
            skLineSegment(sketch, "E40.0.18.8", {"start": v(-25.4, 50.92) * mm, "end": v(-25.4, 49.4) * mm});
            skLineSegment(sketch, "E40.0.18.9", {"start": v(-24.64, 49.4) * mm, "end": v(-0.76, 49.4) * mm});
            skLineSegment(sketch, "E40.0.18.10", {"start": v(-25.4, 51.68) * mm, "end": v(-25.4, 52.44) * mm});
            skLineSegment(sketch, "E40.0.18.11", {"start": v(-13.82, 51.68) * mm, "end": v(-13.82, 50.92) * mm});
            skLineSegment(sketch, "E40.0.18.12", {"start": v(-11.58, 51.68) * mm, "end": v(-11.58, 50.92) * mm});
            skLineSegment(sketch, "E40.0.18.13", {"start": v(-24.64, 50.16) * mm, "end": v(-0.76, 50.16) * mm});
            skLineSegment(sketch, "E40.0.18.14", {"start": v(-25.4, 50.92) * mm, "end": v(-13.82, 50.92) * mm});
            skLineSegment(sketch, "E40.0.19.0", {"start": v(-0.76, 47.1) * mm, "end": v(-0.76, 46.35) * mm});
            skLineSegment(sketch, "E40.0.19.1", {"start": v(0, 48.63) * mm, "end": v(0, 49.4) * mm});
            skPoint(sketch, "E40.0.19.2", {"position": v(0, 49.4) * mm});
            skLineSegment(sketch, "E40.0.19.3", {"start": v(-24.64, 47.1) * mm, "end": v(-24.64, 46.35) * mm});
            skLineSegment(sketch, "E40.0.19.4", {"start": v(0, 48.63) * mm, "end": v(-11.58, 48.63) * mm});
            skLineSegment(sketch, "E40.0.19.5", {"start": v(-25.4, 48.63) * mm, "end": v(-13.82, 48.63) * mm});
            skLineSegment(sketch, "E40.0.19.6", {"start": v(0, 47.87) * mm, "end": v(-11.58, 47.87) * mm});
            skLineSegment(sketch, "E40.0.19.7", {"start": v(0, 47.87) * mm, "end": v(0, 46.35) * mm});
            skLineSegment(sketch, "E40.0.19.8", {"start": v(-25.4, 47.87) * mm, "end": v(-25.4, 46.35) * mm});
            skLineSegment(sketch, "E40.0.19.9", {"start": v(-24.64, 46.35) * mm, "end": v(-0.76, 46.35) * mm});
            skLineSegment(sketch, "E40.0.19.10", {"start": v(-25.4, 48.63) * mm, "end": v(-25.4, 49.4) * mm});
            skLineSegment(sketch, "E40.0.19.11", {"start": v(-13.82, 48.63) * mm, "end": v(-13.82, 47.87) * mm});
            skLineSegment(sketch, "E40.0.19.12", {"start": v(-11.58, 48.63) * mm, "end": v(-11.58, 47.87) * mm});
            skLineSegment(sketch, "E40.0.19.13", {"start": v(-24.64, 47.1) * mm, "end": v(-0.76, 47.1) * mm});
            skLineSegment(sketch, "E40.0.19.14", {"start": v(-25.4, 47.87) * mm, "end": v(-13.82, 47.87) * mm});
            skLineSegment(sketch, "E40.0.20.0", {"start": v(-0.76, 44.06) * mm, "end": v(-0.76, 43.3) * mm});
            skLineSegment(sketch, "E40.0.20.1", {"start": v(0, 45.59) * mm, "end": v(0, 46.35) * mm});
            skPoint(sketch, "E40.0.20.2", {"position": v(0, 46.35) * mm});
            skLineSegment(sketch, "E40.0.20.3", {"start": v(-24.64, 44.06) * mm, "end": v(-24.64, 43.3) * mm});
            skLineSegment(sketch, "E40.0.20.4", {"start": v(0, 45.59) * mm, "end": v(-11.58, 45.59) * mm});
            skLineSegment(sketch, "E40.0.20.5", {"start": v(-25.4, 45.59) * mm, "end": v(-13.82, 45.59) * mm});
            skLineSegment(sketch, "E40.0.20.6", {"start": v(0, 44.82) * mm, "end": v(-11.58, 44.82) * mm});
            skLineSegment(sketch, "E40.0.20.7", {"start": v(0, 44.82) * mm, "end": v(0, 43.3) * mm});
            skLineSegment(sketch, "E40.0.20.8", {"start": v(-25.4, 44.82) * mm, "end": v(-25.4, 43.3) * mm});
            skLineSegment(sketch, "E40.0.20.9", {"start": v(-24.64, 43.3) * mm, "end": v(-0.76, 43.3) * mm});
            skLineSegment(sketch, "E40.0.20.10", {"start": v(-25.4, 45.59) * mm, "end": v(-25.4, 46.35) * mm});
            skLineSegment(sketch, "E40.0.20.11", {"start": v(-13.82, 45.59) * mm, "end": v(-13.82, 44.82) * mm});
            skLineSegment(sketch, "E40.0.20.12", {"start": v(-11.58, 45.59) * mm, "end": v(-11.58, 44.82) * mm});
            skLineSegment(sketch, "E40.0.20.13", {"start": v(-24.64, 44.06) * mm, "end": v(-0.76, 44.06) * mm});
            skLineSegment(sketch, "E40.0.20.14", {"start": v(-25.4, 44.82) * mm, "end": v(-13.82, 44.82) * mm});
            skLineSegment(sketch, "E40.0.21.0", {"start": v(-0.76, 41.01) * mm, "end": v(-0.76, 40.25) * mm});
            skLineSegment(sketch, "E40.0.21.1", {"start": v(0, 42.54) * mm, "end": v(0, 43.3) * mm});
            skPoint(sketch, "E40.0.21.2", {"position": v(0, 43.3) * mm});
            skLineSegment(sketch, "E40.0.21.3", {"start": v(-24.64, 41.01) * mm, "end": v(-24.64, 40.25) * mm});
            skLineSegment(sketch, "E40.0.21.4", {"start": v(0, 42.54) * mm, "end": v(-11.58, 42.54) * mm});
            skLineSegment(sketch, "E40.0.21.5", {"start": v(-25.4, 42.54) * mm, "end": v(-13.82, 42.54) * mm});
            skLineSegment(sketch, "E40.0.21.6", {"start": v(0, 41.78) * mm, "end": v(-11.58, 41.78) * mm});
            skLineSegment(sketch, "E40.0.21.7", {"start": v(0, 41.78) * mm, "end": v(0, 40.25) * mm});
            skLineSegment(sketch, "E40.0.21.8", {"start": v(-25.4, 41.78) * mm, "end": v(-25.4, 40.25) * mm});
            skLineSegment(sketch, "E40.0.21.9", {"start": v(-24.64, 40.25) * mm, "end": v(-0.76, 40.25) * mm});
            skLineSegment(sketch, "E40.0.21.10", {"start": v(-25.4, 42.54) * mm, "end": v(-25.4, 43.3) * mm});
            skLineSegment(sketch, "E40.0.21.11", {"start": v(-13.82, 42.54) * mm, "end": v(-13.82, 41.78) * mm});
            skLineSegment(sketch, "E40.0.21.12", {"start": v(-11.58, 42.54) * mm, "end": v(-11.58, 41.78) * mm});
            skLineSegment(sketch, "E40.0.21.13", {"start": v(-24.64, 41.01) * mm, "end": v(-0.76, 41.01) * mm});
            skLineSegment(sketch, "E40.0.21.14", {"start": v(-25.4, 41.78) * mm, "end": v(-13.82, 41.78) * mm});
            skLineSegment(sketch, "E40.0.22.0", {"start": v(-0.76, 37.97) * mm, "end": v(-0.76, 37.2) * mm});
            skLineSegment(sketch, "E40.0.22.1", {"start": v(0, 39.49) * mm, "end": v(0, 40.25) * mm});
            skPoint(sketch, "E40.0.22.2", {"position": v(0, 40.25) * mm});
            skLineSegment(sketch, "E40.0.22.3", {"start": v(-24.64, 37.97) * mm, "end": v(-24.64, 37.2) * mm});
            skLineSegment(sketch, "E40.0.22.4", {"start": v(0, 39.49) * mm, "end": v(-11.58, 39.49) * mm});
            skLineSegment(sketch, "E40.0.22.5", {"start": v(-25.4, 39.49) * mm, "end": v(-13.82, 39.49) * mm});
            skLineSegment(sketch, "E40.0.22.6", {"start": v(0, 38.73) * mm, "end": v(-11.58, 38.73) * mm});
            skLineSegment(sketch, "E40.0.22.7", {"start": v(0, 38.73) * mm, "end": v(0, 37.2) * mm});
            skLineSegment(sketch, "E40.0.22.8", {"start": v(-25.4, 38.73) * mm, "end": v(-25.4, 37.2) * mm});
            skLineSegment(sketch, "E40.0.22.9", {"start": v(-24.64, 37.2) * mm, "end": v(-0.76, 37.2) * mm});
            skLineSegment(sketch, "E40.0.22.10", {"start": v(-25.4, 39.49) * mm, "end": v(-25.4, 40.25) * mm});
            skLineSegment(sketch, "E40.0.22.11", {"start": v(-13.82, 39.49) * mm, "end": v(-13.82, 38.73) * mm});
            skLineSegment(sketch, "E40.0.22.12", {"start": v(-11.58, 39.49) * mm, "end": v(-11.58, 38.73) * mm});
            skLineSegment(sketch, "E40.0.22.13", {"start": v(-24.64, 37.97) * mm, "end": v(-0.76, 37.97) * mm});
            skLineSegment(sketch, "E40.0.22.14", {"start": v(-25.4, 38.73) * mm, "end": v(-13.82, 38.73) * mm});
            skLineSegment(sketch, "E40.0.23.0", {"start": v(-0.76, 34.92) * mm, "end": v(-0.76, 34.16) * mm});
            skLineSegment(sketch, "E40.0.23.1", {"start": v(0, 36.44) * mm, "end": v(0, 37.2) * mm});
            skPoint(sketch, "E40.0.23.2", {"position": v(0, 37.2) * mm});
            skLineSegment(sketch, "E40.0.23.3", {"start": v(-24.64, 34.92) * mm, "end": v(-24.64, 34.16) * mm});
            skLineSegment(sketch, "E40.0.23.4", {"start": v(0, 36.44) * mm, "end": v(-11.58, 36.44) * mm});
            skLineSegment(sketch, "E40.0.23.5", {"start": v(-25.4, 36.44) * mm, "end": v(-13.82, 36.44) * mm});
            skLineSegment(sketch, "E40.0.23.6", {"start": v(0, 35.68) * mm, "end": v(-11.58, 35.68) * mm});
            skLineSegment(sketch, "E40.0.23.7", {"start": v(0, 35.68) * mm, "end": v(0, 34.16) * mm});
            skLineSegment(sketch, "E40.0.23.8", {"start": v(-25.4, 35.68) * mm, "end": v(-25.4, 34.16) * mm});
            skLineSegment(sketch, "E40.0.23.9", {"start": v(-24.64, 34.16) * mm, "end": v(-0.76, 34.16) * mm});
            skLineSegment(sketch, "E40.0.23.10", {"start": v(-25.4, 36.44) * mm, "end": v(-25.4, 37.2) * mm});
            skLineSegment(sketch, "E40.0.23.11", {"start": v(-13.82, 36.44) * mm, "end": v(-13.82, 35.68) * mm});
            skLineSegment(sketch, "E40.0.23.12", {"start": v(-11.58, 36.44) * mm, "end": v(-11.58, 35.68) * mm});
            skLineSegment(sketch, "E40.0.23.13", {"start": v(-24.64, 34.92) * mm, "end": v(-0.76, 34.92) * mm});
            skLineSegment(sketch, "E40.0.23.14", {"start": v(-25.4, 35.68) * mm, "end": v(-13.82, 35.68) * mm});
            skLineSegment(sketch, "E40.0.24.0", {"start": v(-0.76, 31.87) * mm, "end": v(-0.76, 31.1) * mm});
            skLineSegment(sketch, "E40.0.24.1", {"start": v(0, 33.4) * mm, "end": v(0, 34.16) * mm});
            skPoint(sketch, "E40.0.24.2", {"position": v(0, 34.16) * mm});
            skLineSegment(sketch, "E40.0.24.3", {"start": v(-24.64, 31.87) * mm, "end": v(-24.64, 31.1) * mm});
            skLineSegment(sketch, "E40.0.24.4", {"start": v(0, 33.4) * mm, "end": v(-11.58, 33.4) * mm});
            skLineSegment(sketch, "E40.0.24.5", {"start": v(-25.4, 33.4) * mm, "end": v(-13.82, 33.4) * mm});
            skLineSegment(sketch, "E40.0.24.6", {"start": v(0, 32.63) * mm, "end": v(-11.58, 32.63) * mm});
            skLineSegment(sketch, "E40.0.24.7", {"start": v(0, 32.63) * mm, "end": v(0, 31.1) * mm});
            skLineSegment(sketch, "E40.0.24.8", {"start": v(-25.4, 32.63) * mm, "end": v(-25.4, 31.1) * mm});
            skLineSegment(sketch, "E40.0.24.9", {"start": v(-24.64, 31.1) * mm, "end": v(-0.76, 31.1) * mm});
            skLineSegment(sketch, "E40.0.24.10", {"start": v(-25.4, 33.4) * mm, "end": v(-25.4, 34.16) * mm});
            skLineSegment(sketch, "E40.0.24.11", {"start": v(-13.82, 33.4) * mm, "end": v(-13.82, 32.63) * mm});
            skLineSegment(sketch, "E40.0.24.12", {"start": v(-11.58, 33.4) * mm, "end": v(-11.58, 32.63) * mm});
            skLineSegment(sketch, "E40.0.24.13", {"start": v(-24.64, 31.87) * mm, "end": v(-0.76, 31.87) * mm});
            skLineSegment(sketch, "E40.0.24.14", {"start": v(-25.4, 32.63) * mm, "end": v(-13.82, 32.63) * mm});
            skLineSegment(sketch, "E40.direction1", {"start": v(-25.4, 104.26) * mm, "end": v(-45.16, 104.26) * mm, "construction": true});
            skLineSegment(sketch, "E40.direction2", {"start": v(-25.4, 104.26) * mm, "end": v(-25.4, 101.21) * mm, "construction": true});
            skLineSegment(sketch, "E41", {"start": v(0, 3.8) * mm, "end": v(0, 25.01) * mm});
            skLineSegment(sketch, "E42", {"start": v(-25.4, 3.81) * mm, "end": v(-25.4, 25.01) * mm});
            skLineSegment(sketch, "E43.0.0.25", {"start": v(-0.76, 28.82) * mm, "end": v(-0.76, 28.06) * mm});
            skLineSegment(sketch, "E43.3.0.25", {"start": v(0, 30.35) * mm, "end": v(0, 31.1) * mm});
            skPoint(sketch, "E43.6.0.25", {"position": v(0, 31.1) * mm});
            skLineSegment(sketch, "E43.7.0.25", {"start": v(-24.64, 28.82) * mm, "end": v(-24.64, 28.06) * mm});
            skLineSegment(sketch, "E43.10.0.25", {"start": v(0, 30.35) * mm, "end": v(-11.58, 30.35) * mm});
            skLineSegment(sketch, "E43.13.0.25", {"start": v(-25.4, 30.35) * mm, "end": v(-13.82, 30.35) * mm});
            skLineSegment(sketch, "E43.16.0.25", {"start": v(0, 29.58) * mm, "end": v(-11.58, 29.58) * mm});
            skLineSegment(sketch, "E43.19.0.25", {"start": v(0, 29.58) * mm, "end": v(0, 28.06) * mm});
            skLineSegment(sketch, "E43.22.0.25", {"start": v(-25.4, 29.58) * mm, "end": v(-25.4, 28.06) * mm});
            skLineSegment(sketch, "E43.25.0.25", {"start": v(-24.64, 28.06) * mm, "end": v(-0.76, 28.06) * mm});
            skLineSegment(sketch, "E43.28.0.25", {"start": v(-25.4, 30.35) * mm, "end": v(-25.4, 31.1) * mm});
            skLineSegment(sketch, "E43.31.0.25", {"start": v(-13.82, 30.35) * mm, "end": v(-13.82, 29.58) * mm});
            skLineSegment(sketch, "E43.34.0.25", {"start": v(-11.58, 30.35) * mm, "end": v(-11.58, 29.58) * mm});
            skLineSegment(sketch, "E43.37.0.25", {"start": v(-24.64, 28.82) * mm, "end": v(-0.76, 28.82) * mm});
            skLineSegment(sketch, "E43.40.0.25", {"start": v(-25.4, 29.58) * mm, "end": v(-13.82, 29.58) * mm});
            skLineSegment(sketch, "E43.0.0.26", {"start": v(-0.76, 25.77) * mm, "end": v(-0.76, 25.01) * mm});
            skLineSegment(sketch, "E43.3.0.26", {"start": v(0, 27.3) * mm, "end": v(0, 28.06) * mm});
            skPoint(sketch, "E43.6.0.26", {"position": v(0, 28.06) * mm});
            skLineSegment(sketch, "E43.7.0.26", {"start": v(-24.64, 25.77) * mm, "end": v(-24.64, 25.01) * mm});
            skLineSegment(sketch, "E43.10.0.26", {"start": v(0, 27.3) * mm, "end": v(-11.58, 27.3) * mm});
            skLineSegment(sketch, "E43.13.0.26", {"start": v(-25.4, 27.3) * mm, "end": v(-13.82, 27.3) * mm});
            skLineSegment(sketch, "E43.16.0.26", {"start": v(0, 26.54) * mm, "end": v(-11.58, 26.54) * mm});
            skLineSegment(sketch, "E43.19.0.26", {"start": v(0, 26.54) * mm, "end": v(0, 25.01) * mm});
            skLineSegment(sketch, "E43.22.0.26", {"start": v(-25.4, 26.54) * mm, "end": v(-25.4, 25.01) * mm});
            skLineSegment(sketch, "E43.25.0.26", {"start": v(-24.64, 25.01) * mm, "end": v(-0.76, 25.01) * mm});
            skLineSegment(sketch, "E43.28.0.26", {"start": v(-25.4, 27.3) * mm, "end": v(-25.4, 28.06) * mm});
            skLineSegment(sketch, "E43.31.0.26", {"start": v(-13.82, 27.3) * mm, "end": v(-13.82, 26.54) * mm});
            skLineSegment(sketch, "E43.34.0.26", {"start": v(-11.58, 27.3) * mm, "end": v(-11.58, 26.54) * mm});
            skLineSegment(sketch, "E43.37.0.26", {"start": v(-24.64, 25.77) * mm, "end": v(-0.76, 25.77) * mm});
            skLineSegment(sketch, "E43.40.0.26", {"start": v(-25.4, 26.54) * mm, "end": v(-13.82, 26.54) * mm});
            skPoint(sketch, "E44", {"position": v(-1.9, 15.73) * mm});
            skCircle(sketch, "E45", {"center": v(-1.9, 15.73) * mm, "radius": 1.9 * mm});
            skSolve(sketch);
        }
        {
            var Q0;
            Q0=makeQuery(id+"F2.imprint","IMPRINT",FACE,{"disambiguationData":[TD([[makeQuery(id+"F2.imprint","IMPRINT",EDGE,{"derivedFrom":sQuery(id+"F2.wireOp",EDGE,"E21")}),-1.0]])]});
            var Q1;
            {var subQ3=sQuery(id+"F2.wireOp",EDGE,"E20");Q1=makeQuery(id+"F2.imprint","IMPRINT",FACE,{"disambiguationData":[TD([[makeQuery(id+"F2.imprint","IMPRINT",EDGE,{"derivedFrom":subQ3}),1.0]])]});}
            var Q2;
            Q2=makeQuery(id+"F2.imprint","IMPRINT",FACE,{"disambiguationData":[TD([[makeQuery(id+"F2.imprint","IMPRINT",EDGE,{"derivedFrom":sQuery(id+"F2.wireOp",EDGE,"E24")}),1.0]])]});
            extrude(context, id + "F3", {"entities" : qUnion([Q0, Q1, Q2]), "depth" : 3.8 * mm});
        }
        {
            var Q0;
            Q0=sQuery(id+"F2.wireOp",VERTEX,"E24.center");
            var Q1;
            Q1=makeQuery(id+"F3.opExtrude","SWEPT_BODY",BODY,{"disambiguationData":[OSD([sQuery(id+"F2.wireOp",EDGE,"E19.bottom"),sQuery(id+"F2.wireOp",EDGE,"E19.right"),sQuery(id+"F2.wireOp",EDGE,"E20"),sQuery(id+"F2.wireOp",EDGE,"E21"),sQuery(id+"F2.wireOp",EDGE,"E22.MirrorCS"),sQuery(id+"F2.wireOp",EDGE,"E23.MirrorCS"),sQuery(id+"F2.wireOp",EDGE,"E26"),sQuery(id+"F2.wireOp",EDGE,"E30")])]});
            hole(context, id + "F4", {"style" : HoleStyle.SIMPLE, "endStyle" : HoleEndStyle.THROUGH, "oppositeDirection" : true, "holeDiameter" : 3.78 * mm, "locations" : qUnion([Q0]), "scope" : qUnion([Q1]), "isTappedThrough" : true});
        }
        {
            var Q0;
            Q0=makeQuery(id+"F1.opExtrude","SWEPT_FACE",FACE,{"disambiguationData":[OSD([sQuery(id+"F0.wireOp",EDGE,"E0.right")])]});
            var sketch = newSketch(context, id + "F5", { "sketchPlane" : qUnion([Q0])});
            skLineSegment(sketch, "E46.bottom", {"start": v(0, 3.81) * mm, "end": v(-3.62, 3.81) * mm});
            skLineSegment(sketch, "E46.top", {"start": v(0, 22.86) * mm, "end": v(-46.99, 22.86) * mm});
            skLineSegment(sketch, "E46.left", {"start": v(0, 3.81) * mm, "end": v(0, 22.86) * mm});
            skLineSegment(sketch, "E46.right", {"start": v(-46.99, 3.8) * mm, "end": v(-46.99, 13.82) * mm});
            skLineSegment(sketch, "E47.bottom", {"start": v(-46.99, 13.82) * mm, "end": v(-39.37, 13.82) * mm});
            skLineSegment(sketch, "E47.top", {"start": v(-47, 17.63) * mm, "end": v(-39.37, 17.63) * mm});
            skLineSegment(sketch, "E47.right", {"start": v(-30.48, 13.82) * mm, "end": v(-30.48, 17.63) * mm});
            skLineSegment(sketch, "E48.bottom", {"start": v(-35.56, 18.45) * mm, "end": v(-39.37, 18.45) * mm});
            skLineSegment(sketch, "E48.top", {"start": v(-35.56, 13) * mm, "end": v(-39.37, 13) * mm});
            skLineSegment(sketch, "E48.left", {"start": v(-35.56, 18.45) * mm, "end": v(-35.56, 17.63) * mm});
            skLineSegment(sketch, "E48.right", {"start": v(-39.37, 18.45) * mm, "end": v(-39.37, 17.63) * mm});
            skLineSegment(sketch, "E49.trimOffspring", {"start": v(-39.37, 13.82) * mm, "end": v(-39.37, 13) * mm});
            skLineSegment(sketch, "E50.trimOffspring", {"start": v(-35.56, 13.82) * mm, "end": v(-35.56, 13) * mm});
            skLineSegment(sketch, "E51.trimOffspring", {"start": v(-35.56, 13.82) * mm, "end": v(-30.48, 13.82) * mm});
            skLineSegment(sketch, "E52.trimOffspring", {"start": v(-35.56, 17.63) * mm, "end": v(-30.48, 17.63) * mm});
            skLineSegment(sketch, "E53.bottom", {"start": v(-18.7, 0) * mm, "end": v(-3.62, 0) * mm});
            skLineSegment(sketch, "E53.left", {"start": v(-18.7, 0) * mm, "end": v(-18.7, 3.81) * mm});
            skLineSegment(sketch, "E53.right", {"start": v(-3.62, 0) * mm, "end": v(-3.62, 3.81) * mm});
            skLineSegment(sketch, "E54.trimOffspring", {"start": v(-18.7, 3.8) * mm, "end": v(-46.99, 3.8) * mm});
            skLineSegment(sketch, "E55.trimOffspring", {"start": v(-46.99, 17.63) * mm, "end": v(-46.99, 22.86) * mm});
            skLineSegment(sketch, "E56", {"start": v(-11.8, 0) * mm, "end": v(-11.8, 3.81) * mm, "construction": true});
            skLineSegment(sketch, "E57", {"start": v(-13.7, 1.9) * mm, "end": v(-9.89, 1.9) * mm, "construction": true});
            skPoint(sketch, "E58", {"position": v(-11.8, 1.9) * mm});
            skCircle(sketch, "E59", {"center": v(-11.8, 1.9) * mm, "radius": 1.9 * mm});
            skSolve(sketch);
        }
        {
            var Q0;
            Q0 = qSketchRegion(id + "F5", true);
            extrude(context, id + "F6", {"entities" : qUnion([Q0]), "oppositeDirection" : true, "depth" : 3.8 * mm});
        }
        {
            var Q0;
            Q0=sQuery(id+"F5.wireOp",VERTEX,"E58");
            var Q1;
            Q1=makeQuery(id+"F6.opExtrude","SWEPT_BODY",BODY,{"disambiguationData":[OSD([sQuery(id+"F5.wireOp",EDGE,"E46.bottom"),sQuery(id+"F5.wireOp",EDGE,"E46.top"),sQuery(id+"F5.wireOp",EDGE,"E46.left"),sQuery(id+"F5.wireOp",EDGE,"E46.right"),sQuery(id+"F5.wireOp",EDGE,"E47.bottom"),sQuery(id+"F5.wireOp",EDGE,"E47.top"),sQuery(id+"F5.wireOp",EDGE,"E47.right"),sQuery(id+"F5.wireOp",EDGE,"E48.bottom"),sQuery(id+"F5.wireOp",EDGE,"E48.top"),sQuery(id+"F5.wireOp",EDGE,"E48.left"),sQuery(id+"F5.wireOp",EDGE,"E48.right"),sQuery(id+"F5.wireOp",EDGE,"E49.trimOffspring"),sQuery(id+"F5.wireOp",EDGE,"E50.trimOffspring"),sQuery(id+"F5.wireOp",EDGE,"E51.trimOffspring"),sQuery(id+"F5.wireOp",EDGE,"E52.trimOffspring"),sQuery(id+"F5.wireOp",EDGE,"E53.bottom"),sQuery(id+"F5.wireOp",EDGE,"E53.left"),sQuery(id+"F5.wireOp",EDGE,"E53.right"),sQuery(id+"F5.wireOp",EDGE,"E54.trimOffspring"),sQuery(id+"F5.wireOp",EDGE,"E55.trimOffspring")])]});
            hole(context, id + "F7", {"style" : HoleStyle.SIMPLE, "endStyle" : HoleEndStyle.THROUGH, "holeDiameter" : 3.78 * mm, "locations" : qUnion([Q0]), "scope" : qUnion([Q1]), "isTappedThrough" : true});
        }
        {
            var Q0;
            Q0=sQuery(id+"F2.wireOp",VERTEX,"E44");
            var Q1;
            Q1=makeQuery(id+"F3.opExtrude","SWEPT_BODY",BODY,{"disambiguationData":[OSD([sQuery(id+"F2.wireOp",EDGE,"E19.bottom"),sQuery(id+"F2.wireOp",EDGE,"E20"),sQuery(id+"F2.wireOp",EDGE,"E21"),sQuery(id+"F2.wireOp",EDGE,"E22.MirrorCS"),sQuery(id+"F2.wireOp",EDGE,"E23.MirrorCS"),sQuery(id+"F2.wireOp",EDGE,"E26"),sQuery(id+"F2.wireOp",EDGE,"E28.bottom"),sQuery(id+"F2.wireOp",EDGE,"E28.top"),sQuery(id+"F2.wireOp",EDGE,"E28.right"),sQuery(id+"F2.wireOp",EDGE,"E29.trimOffspring"),sQuery(id+"F2.wireOp",EDGE,"E31.MirrorCS"),sQuery(id+"F2.wireOp",EDGE,"E32.MirrorCS"),sQuery(id+"F2.wireOp",EDGE,"E33.MirrorCS"),sQuery(id+"F2.wireOp",EDGE,"E34.MirrorCS"),sQuery(id+"F2.wireOp",EDGE,"E35.MirrorCS"),sQuery(id+"F2.wireOp",EDGE,"E36.bottom"),sQuery(id+"F2.wireOp",EDGE,"E36.top"),sQuery(id+"F2.wireOp",EDGE,"E36.left"),sQuery(id+"F2.wireOp",EDGE,"E36.right"),sQuery(id+"F2.wireOp",EDGE,"E37"),sQuery(id+"F2.wireOp",EDGE,"E39.MirrorCS"),sQuery(id+"F2.wireOp",EDGE,"E40.0.1.0"),sQuery(id+"F2.wireOp",EDGE,"E40.0.1.1"),sQuery(id+"F2.wireOp",EDGE,"E40.0.1.3"),sQuery(id+"F2.wireOp",EDGE,"E40.0.1.4"),sQuery(id+"F2.wireOp",EDGE,"E40.0.1.5"),sQuery(id+"F2.wireOp",EDGE,"E40.0.1.6"),sQuery(id+"F2.wireOp",EDGE,"E40.0.1.7"),sQuery(id+"F2.wireOp",EDGE,"E40.0.1.8"),sQuery(id+"F2.wireOp",EDGE,"E40.0.1.9"),sQuery(id+"F2.wireOp",EDGE,"E40.0.1.10"),sQuery(id+"F2.wireOp",EDGE,"E40.0.1.11"),sQuery(id+"F2.wireOp",EDGE,"E40.0.1.12"),sQuery(id+"F2.wireOp",EDGE,"E40.0.1.13"),sQuery(id+"F2.wireOp",EDGE,"E40.0.1.14"),sQuery(id+"F2.wireOp",EDGE,"E40.0.2.0"),sQuery(id+"F2.wireOp",EDGE,"E40.0.2.1"),sQuery(id+"F2.wireOp",EDGE,"E40.0.2.3"),sQuery(id+"F2.wireOp",EDGE,"E40.0.2.4"),sQuery(id+"F2.wireOp",EDGE,"E40.0.2.5"),sQuery(id+"F2.wireOp",EDGE,"E40.0.2.6"),sQuery(id+"F2.wireOp",EDGE,"E40.0.2.7"),sQuery(id+"F2.wireOp",EDGE,"E40.0.2.8"),sQuery(id+"F2.wireOp",EDGE,"E40.0.2.9"),sQuery(id+"F2.wireOp",EDGE,"E40.0.2.10"),sQuery(id+"F2.wireOp",EDGE,"E40.0.2.11"),sQuery(id+"F2.wireOp",EDGE,"E40.0.2.12"),sQuery(id+"F2.wireOp",EDGE,"E40.0.2.13"),sQuery(id+"F2.wireOp",EDGE,"E40.0.2.14"),sQuery(id+"F2.wireOp",EDGE,"E40.0.3.0"),sQuery(id+"F2.wireOp",EDGE,"E40.0.3.1"),sQuery(id+"F2.wireOp",EDGE,"E40.0.3.3"),sQuery(id+"F2.wireOp",EDGE,"E40.0.3.4"),sQuery(id+"F2.wireOp",EDGE,"E40.0.3.5"),sQuery(id+"F2.wireOp",EDGE,"E40.0.3.6"),sQuery(id+"F2.wireOp",EDGE,"E40.0.3.7"),sQuery(id+"F2.wireOp",EDGE,"E40.0.3.8"),sQuery(id+"F2.wireOp",EDGE,"E40.0.3.9"),sQuery(id+"F2.wireOp",EDGE,"E40.0.3.10"),sQuery(id+"F2.wireOp",EDGE,"E40.0.3.11"),sQuery(id+"F2.wireOp",EDGE,"E40.0.3.12"),sQuery(id+"F2.wireOp",EDGE,"E40.0.3.13"),sQuery(id+"F2.wireOp",EDGE,"E40.0.3.14"),sQuery(id+"F2.wireOp",EDGE,"E40.0.4.0"),sQuery(id+"F2.wireOp",EDGE,"E40.0.4.1"),sQuery(id+"F2.wireOp",EDGE,"E40.0.4.3"),sQuery(id+"F2.wireOp",EDGE,"E40.0.4.4"),sQuery(id+"F2.wireOp",EDGE,"E40.0.4.5"),sQuery(id+"F2.wireOp",EDGE,"E40.0.4.6"),sQuery(id+"F2.wireOp",EDGE,"E40.0.4.7"),sQuery(id+"F2.wireOp",EDGE,"E40.0.4.8"),sQuery(id+"F2.wireOp",EDGE,"E40.0.4.9"),sQuery(id+"F2.wireOp",EDGE,"E40.0.4.10"),sQuery(id+"F2.wireOp",EDGE,"E40.0.4.11"),sQuery(id+"F2.wireOp",EDGE,"E40.0.4.12"),sQuery(id+"F2.wireOp",EDGE,"E40.0.4.13"),sQuery(id+"F2.wireOp",EDGE,"E40.0.4.14"),sQuery(id+"F2.wireOp",EDGE,"E40.0.5.0"),sQuery(id+"F2.wireOp",EDGE,"E40.0.5.1"),sQuery(id+"F2.wireOp",EDGE,"E40.0.5.3"),sQuery(id+"F2.wireOp",EDGE,"E40.0.5.4"),sQuery(id+"F2.wireOp",EDGE,"E40.0.5.5"),sQuery(id+"F2.wireOp",EDGE,"E40.0.5.6"),sQuery(id+"F2.wireOp",EDGE,"E40.0.5.7"),sQuery(id+"F2.wireOp",EDGE,"E40.0.5.8"),sQuery(id+"F2.wireOp",EDGE,"E40.0.5.9"),sQuery(id+"F2.wireOp",EDGE,"E40.0.5.10"),sQuery(id+"F2.wireOp",EDGE,"E40.0.5.11"),sQuery(id+"F2.wireOp",EDGE,"E40.0.5.12"),sQuery(id+"F2.wireOp",EDGE,"E40.0.5.13"),sQuery(id+"F2.wireOp",EDGE,"E40.0.5.14"),sQuery(id+"F2.wireOp",EDGE,"E40.0.6.0"),sQuery(id+"F2.wireOp",EDGE,"E40.0.6.1"),sQuery(id+"F2.wireOp",EDGE,"E40.0.6.3"),sQuery(id+"F2.wireOp",EDGE,"E40.0.6.4"),sQuery(id+"F2.wireOp",EDGE,"E40.0.6.5"),sQuery(id+"F2.wireOp",EDGE,"E40.0.6.6"),sQuery(id+"F2.wireOp",EDGE,"E40.0.6.7"),sQuery(id+"F2.wireOp",EDGE,"E40.0.6.8"),sQuery(id+"F2.wireOp",EDGE,"E40.0.6.9"),sQuery(id+"F2.wireOp",EDGE,"E40.0.6.10"),sQuery(id+"F2.wireOp",EDGE,"E40.0.6.11"),sQuery(id+"F2.wireOp",EDGE,"E40.0.6.12"),sQuery(id+"F2.wireOp",EDGE,"E40.0.6.13"),sQuery(id+"F2.wireOp",EDGE,"E40.0.6.14"),sQuery(id+"F2.wireOp",EDGE,"E40.0.7.0"),sQuery(id+"F2.wireOp",EDGE,"E40.0.7.1"),sQuery(id+"F2.wireOp",EDGE,"E40.0.7.3"),sQuery(id+"F2.wireOp",EDGE,"E40.0.7.4"),sQuery(id+"F2.wireOp",EDGE,"E40.0.7.5"),sQuery(id+"F2.wireOp",EDGE,"E40.0.7.6"),sQuery(id+"F2.wireOp",EDGE,"E40.0.7.7"),sQuery(id+"F2.wireOp",EDGE,"E40.0.7.8"),sQuery(id+"F2.wireOp",EDGE,"E40.0.7.9"),sQuery(id+"F2.wireOp",EDGE,"E40.0.7.10"),sQuery(id+"F2.wireOp",EDGE,"E40.0.7.11"),sQuery(id+"F2.wireOp",EDGE,"E40.0.7.12"),sQuery(id+"F2.wireOp",EDGE,"E40.0.7.13"),sQuery(id+"F2.wireOp",EDGE,"E40.0.7.14"),sQuery(id+"F2.wireOp",EDGE,"E40.0.8.0"),sQuery(id+"F2.wireOp",EDGE,"E40.0.8.1"),sQuery(id+"F2.wireOp",EDGE,"E40.0.8.3"),sQuery(id+"F2.wireOp",EDGE,"E40.0.8.4"),sQuery(id+"F2.wireOp",EDGE,"E40.0.8.5"),sQuery(id+"F2.wireOp",EDGE,"E40.0.8.6"),sQuery(id+"F2.wireOp",EDGE,"E40.0.8.7"),sQuery(id+"F2.wireOp",EDGE,"E40.0.8.8"),sQuery(id+"F2.wireOp",EDGE,"E40.0.8.9"),sQuery(id+"F2.wireOp",EDGE,"E40.0.8.10"),sQuery(id+"F2.wireOp",EDGE,"E40.0.8.11"),sQuery(id+"F2.wireOp",EDGE,"E40.0.8.12"),sQuery(id+"F2.wireOp",EDGE,"E40.0.8.13"),sQuery(id+"F2.wireOp",EDGE,"E40.0.8.14"),sQuery(id+"F2.wireOp",EDGE,"E40.0.9.0"),sQuery(id+"F2.wireOp",EDGE,"E40.0.9.1"),sQuery(id+"F2.wireOp",EDGE,"E40.0.9.3"),sQuery(id+"F2.wireOp",EDGE,"E40.0.9.4"),sQuery(id+"F2.wireOp",EDGE,"E40.0.9.5"),sQuery(id+"F2.wireOp",EDGE,"E40.0.9.6"),sQuery(id+"F2.wireOp",EDGE,"E40.0.9.7"),sQuery(id+"F2.wireOp",EDGE,"E40.0.9.8"),sQuery(id+"F2.wireOp",EDGE,"E40.0.9.9"),sQuery(id+"F2.wireOp",EDGE,"E40.0.9.10"),sQuery(id+"F2.wireOp",EDGE,"E40.0.9.11"),sQuery(id+"F2.wireOp",EDGE,"E40.0.9.12"),sQuery(id+"F2.wireOp",EDGE,"E40.0.9.13"),sQuery(id+"F2.wireOp",EDGE,"E40.0.9.14"),sQuery(id+"F2.wireOp",EDGE,"E40.0.10.0"),sQuery(id+"F2.wireOp",EDGE,"E40.0.10.1"),sQuery(id+"F2.wireOp",EDGE,"E40.0.10.3"),sQuery(id+"F2.wireOp",EDGE,"E40.0.10.4"),sQuery(id+"F2.wireOp",EDGE,"E40.0.10.5"),sQuery(id+"F2.wireOp",EDGE,"E40.0.10.6"),sQuery(id+"F2.wireOp",EDGE,"E40.0.10.7"),sQuery(id+"F2.wireOp",EDGE,"E40.0.10.8"),sQuery(id+"F2.wireOp",EDGE,"E40.0.10.9"),sQuery(id+"F2.wireOp",EDGE,"E40.0.10.10"),sQuery(id+"F2.wireOp",EDGE,"E40.0.10.11"),sQuery(id+"F2.wireOp",EDGE,"E40.0.10.12"),sQuery(id+"F2.wireOp",EDGE,"E40.0.10.13"),sQuery(id+"F2.wireOp",EDGE,"E40.0.10.14"),sQuery(id+"F2.wireOp",EDGE,"E40.0.11.0"),sQuery(id+"F2.wireOp",EDGE,"E40.0.11.1"),sQuery(id+"F2.wireOp",EDGE,"E40.0.11.3"),sQuery(id+"F2.wireOp",EDGE,"E40.0.11.4"),sQuery(id+"F2.wireOp",EDGE,"E40.0.11.5"),sQuery(id+"F2.wireOp",EDGE,"E40.0.11.6"),sQuery(id+"F2.wireOp",EDGE,"E40.0.11.7"),sQuery(id+"F2.wireOp",EDGE,"E40.0.11.8"),sQuery(id+"F2.wireOp",EDGE,"E40.0.11.9"),sQuery(id+"F2.wireOp",EDGE,"E40.0.11.10"),sQuery(id+"F2.wireOp",EDGE,"E40.0.11.11"),sQuery(id+"F2.wireOp",EDGE,"E40.0.11.12"),sQuery(id+"F2.wireOp",EDGE,"E40.0.11.13"),sQuery(id+"F2.wireOp",EDGE,"E40.0.11.14"),sQuery(id+"F2.wireOp",EDGE,"E40.0.12.0"),sQuery(id+"F2.wireOp",EDGE,"E40.0.12.1"),sQuery(id+"F2.wireOp",EDGE,"E40.0.12.3"),sQuery(id+"F2.wireOp",EDGE,"E40.0.12.4"),sQuery(id+"F2.wireOp",EDGE,"E40.0.12.5"),sQuery(id+"F2.wireOp",EDGE,"E40.0.12.6"),sQuery(id+"F2.wireOp",EDGE,"E40.0.12.7"),sQuery(id+"F2.wireOp",EDGE,"E40.0.12.8"),sQuery(id+"F2.wireOp",EDGE,"E40.0.12.9"),sQuery(id+"F2.wireOp",EDGE,"E40.0.12.10"),sQuery(id+"F2.wireOp",EDGE,"E40.0.12.11"),sQuery(id+"F2.wireOp",EDGE,"E40.0.12.12"),sQuery(id+"F2.wireOp",EDGE,"E40.0.12.13"),sQuery(id+"F2.wireOp",EDGE,"E40.0.12.14"),sQuery(id+"F2.wireOp",EDGE,"E40.0.13.0"),sQuery(id+"F2.wireOp",EDGE,"E40.0.13.1"),sQuery(id+"F2.wireOp",EDGE,"E40.0.13.3"),sQuery(id+"F2.wireOp",EDGE,"E40.0.13.4"),sQuery(id+"F2.wireOp",EDGE,"E40.0.13.5"),sQuery(id+"F2.wireOp",EDGE,"E40.0.13.6"),sQuery(id+"F2.wireOp",EDGE,"E40.0.13.7"),sQuery(id+"F2.wireOp",EDGE,"E40.0.13.8"),sQuery(id+"F2.wireOp",EDGE,"E40.0.13.9"),sQuery(id+"F2.wireOp",EDGE,"E40.0.13.10"),sQuery(id+"F2.wireOp",EDGE,"E40.0.13.11"),sQuery(id+"F2.wireOp",EDGE,"E40.0.13.12"),sQuery(id+"F2.wireOp",EDGE,"E40.0.13.13"),sQuery(id+"F2.wireOp",EDGE,"E40.0.13.14"),sQuery(id+"F2.wireOp",EDGE,"E40.0.14.0"),sQuery(id+"F2.wireOp",EDGE,"E40.0.14.1"),sQuery(id+"F2.wireOp",EDGE,"E40.0.14.3"),sQuery(id+"F2.wireOp",EDGE,"E40.0.14.4"),sQuery(id+"F2.wireOp",EDGE,"E40.0.14.5"),sQuery(id+"F2.wireOp",EDGE,"E40.0.14.6"),sQuery(id+"F2.wireOp",EDGE,"E40.0.14.7"),sQuery(id+"F2.wireOp",EDGE,"E40.0.14.8"),sQuery(id+"F2.wireOp",EDGE,"E40.0.14.9"),sQuery(id+"F2.wireOp",EDGE,"E40.0.14.10"),sQuery(id+"F2.wireOp",EDGE,"E40.0.14.11"),sQuery(id+"F2.wireOp",EDGE,"E40.0.14.12"),sQuery(id+"F2.wireOp",EDGE,"E40.0.14.13"),sQuery(id+"F2.wireOp",EDGE,"E40.0.14.14"),sQuery(id+"F2.wireOp",EDGE,"E40.0.15.0"),sQuery(id+"F2.wireOp",EDGE,"E40.0.15.1"),sQuery(id+"F2.wireOp",EDGE,"E40.0.15.3"),sQuery(id+"F2.wireOp",EDGE,"E40.0.15.4"),sQuery(id+"F2.wireOp",EDGE,"E40.0.15.5"),sQuery(id+"F2.wireOp",EDGE,"E40.0.15.6"),sQuery(id+"F2.wireOp",EDGE,"E40.0.15.7"),sQuery(id+"F2.wireOp",EDGE,"E40.0.15.8"),sQuery(id+"F2.wireOp",EDGE,"E40.0.15.9"),sQuery(id+"F2.wireOp",EDGE,"E40.0.15.10"),sQuery(id+"F2.wireOp",EDGE,"E40.0.15.11"),sQuery(id+"F2.wireOp",EDGE,"E40.0.15.12"),sQuery(id+"F2.wireOp",EDGE,"E40.0.15.13"),sQuery(id+"F2.wireOp",EDGE,"E40.0.15.14"),sQuery(id+"F2.wireOp",EDGE,"E40.0.16.0"),sQuery(id+"F2.wireOp",EDGE,"E40.0.16.1"),sQuery(id+"F2.wireOp",EDGE,"E40.0.16.3"),sQuery(id+"F2.wireOp",EDGE,"E40.0.16.4"),sQuery(id+"F2.wireOp",EDGE,"E40.0.16.5"),sQuery(id+"F2.wireOp",EDGE,"E40.0.16.6"),sQuery(id+"F2.wireOp",EDGE,"E40.0.16.7"),sQuery(id+"F2.wireOp",EDGE,"E40.0.16.8"),sQuery(id+"F2.wireOp",EDGE,"E40.0.16.9"),sQuery(id+"F2.wireOp",EDGE,"E40.0.16.10"),sQuery(id+"F2.wireOp",EDGE,"E40.0.16.11"),sQuery(id+"F2.wireOp",EDGE,"E40.0.16.12"),sQuery(id+"F2.wireOp",EDGE,"E40.0.16.13"),sQuery(id+"F2.wireOp",EDGE,"E40.0.16.14"),sQuery(id+"F2.wireOp",EDGE,"E40.0.17.0"),sQuery(id+"F2.wireOp",EDGE,"E40.0.17.1"),sQuery(id+"F2.wireOp",EDGE,"E40.0.17.3"),sQuery(id+"F2.wireOp",EDGE,"E40.0.17.4"),sQuery(id+"F2.wireOp",EDGE,"E40.0.17.5"),sQuery(id+"F2.wireOp",EDGE,"E40.0.17.6"),sQuery(id+"F2.wireOp",EDGE,"E40.0.17.7"),sQuery(id+"F2.wireOp",EDGE,"E40.0.17.8"),sQuery(id+"F2.wireOp",EDGE,"E40.0.17.9"),sQuery(id+"F2.wireOp",EDGE,"E40.0.17.10"),sQuery(id+"F2.wireOp",EDGE,"E40.0.17.11"),sQuery(id+"F2.wireOp",EDGE,"E40.0.17.12"),sQuery(id+"F2.wireOp",EDGE,"E40.0.17.13"),sQuery(id+"F2.wireOp",EDGE,"E40.0.17.14"),sQuery(id+"F2.wireOp",EDGE,"E40.0.18.0"),sQuery(id+"F2.wireOp",EDGE,"E40.0.18.1"),sQuery(id+"F2.wireOp",EDGE,"E40.0.18.3"),sQuery(id+"F2.wireOp",EDGE,"E40.0.18.4"),sQuery(id+"F2.wireOp",EDGE,"E40.0.18.5"),sQuery(id+"F2.wireOp",EDGE,"E40.0.18.6"),sQuery(id+"F2.wireOp",EDGE,"E40.0.18.7"),sQuery(id+"F2.wireOp",EDGE,"E40.0.18.8"),sQuery(id+"F2.wireOp",EDGE,"E40.0.18.9"),sQuery(id+"F2.wireOp",EDGE,"E40.0.18.10"),sQuery(id+"F2.wireOp",EDGE,"E40.0.18.11"),sQuery(id+"F2.wireOp",EDGE,"E40.0.18.12"),sQuery(id+"F2.wireOp",EDGE,"E40.0.18.13"),sQuery(id+"F2.wireOp",EDGE,"E40.0.18.14"),sQuery(id+"F2.wireOp",EDGE,"E40.0.19.0"),sQuery(id+"F2.wireOp",EDGE,"E40.0.19.1"),sQuery(id+"F2.wireOp",EDGE,"E40.0.19.3"),sQuery(id+"F2.wireOp",EDGE,"E40.0.19.4"),sQuery(id+"F2.wireOp",EDGE,"E40.0.19.5"),sQuery(id+"F2.wireOp",EDGE,"E40.0.19.6"),sQuery(id+"F2.wireOp",EDGE,"E40.0.19.7"),sQuery(id+"F2.wireOp",EDGE,"E40.0.19.8"),sQuery(id+"F2.wireOp",EDGE,"E40.0.19.9"),sQuery(id+"F2.wireOp",EDGE,"E40.0.19.10"),sQuery(id+"F2.wireOp",EDGE,"E40.0.19.11"),sQuery(id+"F2.wireOp",EDGE,"E40.0.19.12"),sQuery(id+"F2.wireOp",EDGE,"E40.0.19.13"),sQuery(id+"F2.wireOp",EDGE,"E40.0.19.14"),sQuery(id+"F2.wireOp",EDGE,"E40.0.20.0"),sQuery(id+"F2.wireOp",EDGE,"E40.0.20.1"),sQuery(id+"F2.wireOp",EDGE,"E40.0.20.3"),sQuery(id+"F2.wireOp",EDGE,"E40.0.20.4"),sQuery(id+"F2.wireOp",EDGE,"E40.0.20.5"),sQuery(id+"F2.wireOp",EDGE,"E40.0.20.6"),sQuery(id+"F2.wireOp",EDGE,"E40.0.20.7"),sQuery(id+"F2.wireOp",EDGE,"E40.0.20.8"),sQuery(id+"F2.wireOp",EDGE,"E40.0.20.9"),sQuery(id+"F2.wireOp",EDGE,"E40.0.20.10"),sQuery(id+"F2.wireOp",EDGE,"E40.0.20.11"),sQuery(id+"F2.wireOp",EDGE,"E40.0.20.12"),sQuery(id+"F2.wireOp",EDGE,"E40.0.20.13"),sQuery(id+"F2.wireOp",EDGE,"E40.0.20.14"),sQuery(id+"F2.wireOp",EDGE,"E40.0.21.0"),sQuery(id+"F2.wireOp",EDGE,"E40.0.21.1"),sQuery(id+"F2.wireOp",EDGE,"E40.0.21.3"),sQuery(id+"F2.wireOp",EDGE,"E40.0.21.4"),sQuery(id+"F2.wireOp",EDGE,"E40.0.21.5"),sQuery(id+"F2.wireOp",EDGE,"E40.0.21.6"),sQuery(id+"F2.wireOp",EDGE,"E40.0.21.7"),sQuery(id+"F2.wireOp",EDGE,"E40.0.21.8"),sQuery(id+"F2.wireOp",EDGE,"E40.0.21.9"),sQuery(id+"F2.wireOp",EDGE,"E40.0.21.10"),sQuery(id+"F2.wireOp",EDGE,"E40.0.21.11"),sQuery(id+"F2.wireOp",EDGE,"E40.0.21.12"),sQuery(id+"F2.wireOp",EDGE,"E40.0.21.13"),sQuery(id+"F2.wireOp",EDGE,"E40.0.21.14"),sQuery(id+"F2.wireOp",EDGE,"E40.0.22.0"),sQuery(id+"F2.wireOp",EDGE,"E40.0.22.1"),sQuery(id+"F2.wireOp",EDGE,"E40.0.22.3"),sQuery(id+"F2.wireOp",EDGE,"E40.0.22.4"),sQuery(id+"F2.wireOp",EDGE,"E40.0.22.5"),sQuery(id+"F2.wireOp",EDGE,"E40.0.22.6"),sQuery(id+"F2.wireOp",EDGE,"E40.0.22.7"),sQuery(id+"F2.wireOp",EDGE,"E40.0.22.8"),sQuery(id+"F2.wireOp",EDGE,"E40.0.22.9"),sQuery(id+"F2.wireOp",EDGE,"E40.0.22.10"),sQuery(id+"F2.wireOp",EDGE,"E40.0.22.11"),sQuery(id+"F2.wireOp",EDGE,"E40.0.22.12"),sQuery(id+"F2.wireOp",EDGE,"E40.0.22.13"),sQuery(id+"F2.wireOp",EDGE,"E40.0.22.14"),sQuery(id+"F2.wireOp",EDGE,"E40.0.23.0"),sQuery(id+"F2.wireOp",EDGE,"E40.0.23.1"),sQuery(id+"F2.wireOp",EDGE,"E40.0.23.3"),sQuery(id+"F2.wireOp",EDGE,"E40.0.23.4"),sQuery(id+"F2.wireOp",EDGE,"E40.0.23.5"),sQuery(id+"F2.wireOp",EDGE,"E40.0.23.6"),sQuery(id+"F2.wireOp",EDGE,"E40.0.23.7"),sQuery(id+"F2.wireOp",EDGE,"E40.0.23.8"),sQuery(id+"F2.wireOp",EDGE,"E40.0.23.9"),sQuery(id+"F2.wireOp",EDGE,"E40.0.23.10"),sQuery(id+"F2.wireOp",EDGE,"E40.0.23.11"),sQuery(id+"F2.wireOp",EDGE,"E40.0.23.12"),sQuery(id+"F2.wireOp",EDGE,"E40.0.23.13"),sQuery(id+"F2.wireOp",EDGE,"E40.0.23.14"),sQuery(id+"F2.wireOp",EDGE,"E40.0.24.0"),sQuery(id+"F2.wireOp",EDGE,"E40.0.24.1"),sQuery(id+"F2.wireOp",EDGE,"E40.0.24.3"),sQuery(id+"F2.wireOp",EDGE,"E40.0.24.4"),sQuery(id+"F2.wireOp",EDGE,"E40.0.24.5"),sQuery(id+"F2.wireOp",EDGE,"E40.0.24.6"),sQuery(id+"F2.wireOp",EDGE,"E40.0.24.7"),sQuery(id+"F2.wireOp",EDGE,"E40.0.24.8"),sQuery(id+"F2.wireOp",EDGE,"E40.0.24.9"),sQuery(id+"F2.wireOp",EDGE,"E40.0.24.10"),sQuery(id+"F2.wireOp",EDGE,"E40.0.24.11"),sQuery(id+"F2.wireOp",EDGE,"E40.0.24.12"),sQuery(id+"F2.wireOp",EDGE,"E40.0.24.13"),sQuery(id+"F2.wireOp",EDGE,"E40.0.24.14"),sQuery(id+"F2.wireOp",EDGE,"E41"),sQuery(id+"F2.wireOp",EDGE,"E42"),sQuery(id+"F2.wireOp",EDGE,"E43.0.0.25"),sQuery(id+"F2.wireOp",EDGE,"E43.3.0.25"),sQuery(id+"F2.wireOp",EDGE,"E43.7.0.25"),sQuery(id+"F2.wireOp",EDGE,"E43.10.0.25"),sQuery(id+"F2.wireOp",EDGE,"E43.13.0.25"),sQuery(id+"F2.wireOp",EDGE,"E43.16.0.25"),sQuery(id+"F2.wireOp",EDGE,"E43.19.0.25"),sQuery(id+"F2.wireOp",EDGE,"E43.22.0.25"),sQuery(id+"F2.wireOp",EDGE,"E43.25.0.25"),sQuery(id+"F2.wireOp",EDGE,"E43.28.0.25"),sQuery(id+"F2.wireOp",EDGE,"E43.31.0.25"),sQuery(id+"F2.wireOp",EDGE,"E43.34.0.25"),sQuery(id+"F2.wireOp",EDGE,"E43.37.0.25"),sQuery(id+"F2.wireOp",EDGE,"E43.40.0.25"),sQuery(id+"F2.wireOp",EDGE,"E43.0.0.26"),sQuery(id+"F2.wireOp",EDGE,"E43.3.0.26"),sQuery(id+"F2.wireOp",EDGE,"E43.7.0.26"),sQuery(id+"F2.wireOp",EDGE,"E43.10.0.26"),sQuery(id+"F2.wireOp",EDGE,"E43.13.0.26"),sQuery(id+"F2.wireOp",EDGE,"E43.16.0.26"),sQuery(id+"F2.wireOp",EDGE,"E43.19.0.26"),sQuery(id+"F2.wireOp",EDGE,"E43.22.0.26"),sQuery(id+"F2.wireOp",EDGE,"E43.25.0.26"),sQuery(id+"F2.wireOp",EDGE,"E43.28.0.26"),sQuery(id+"F2.wireOp",EDGE,"E43.31.0.26"),sQuery(id+"F2.wireOp",EDGE,"E43.34.0.26"),sQuery(id+"F2.wireOp",EDGE,"E43.37.0.26"),sQuery(id+"F2.wireOp",EDGE,"E43.40.0.26")])]});
            hole(context, id + "F8", {"style" : HoleStyle.SIMPLE, "endStyle" : HoleEndStyle.THROUGH, "oppositeDirection" : true, "holeDiameter" : 3.78 * mm, "locations" : qUnion([Q0]), "scope" : qUnion([Q1]), "isTappedThrough" : true});
        }
    });
